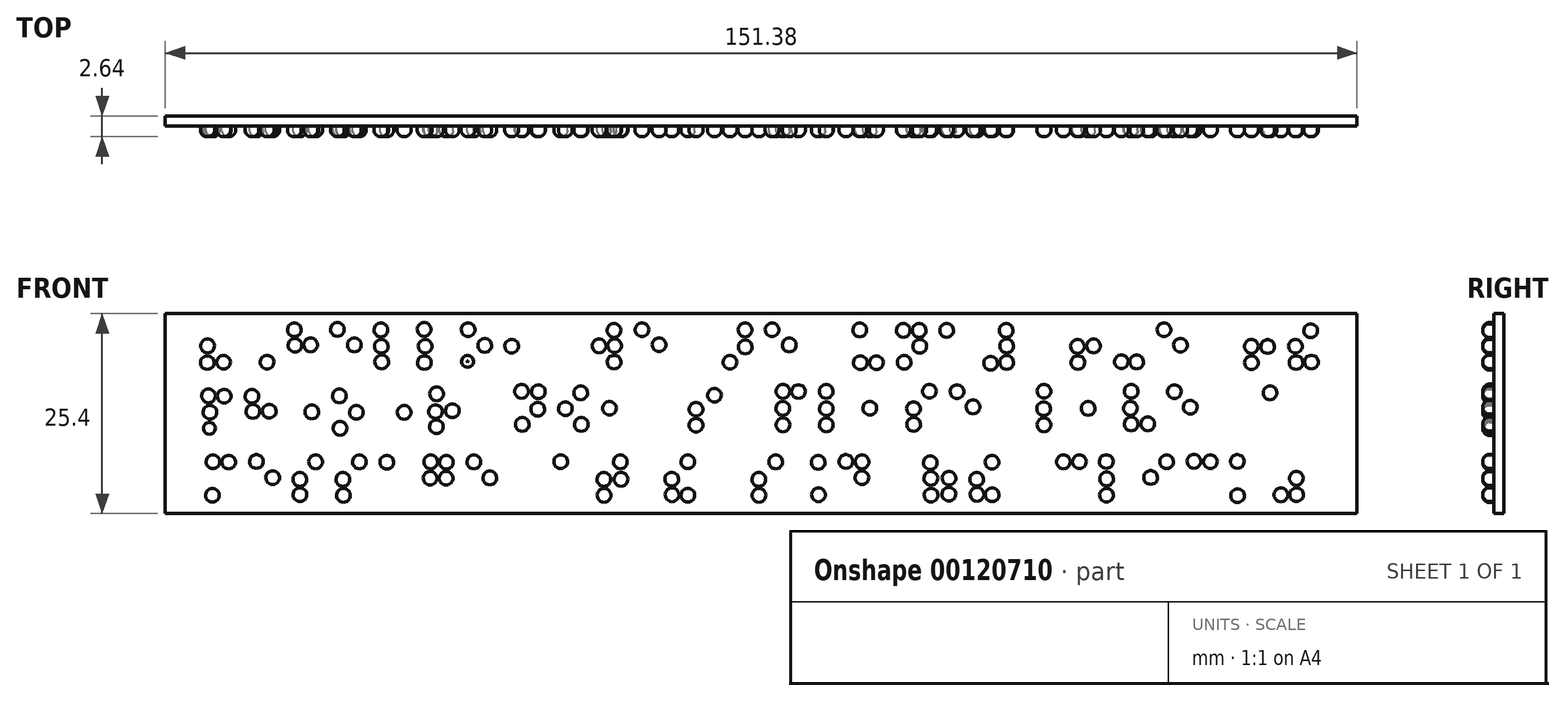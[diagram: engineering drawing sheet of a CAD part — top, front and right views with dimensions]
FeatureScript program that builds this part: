
annotation { "Feature Type Name" : "Feature", "Feature Type Description" : "" }
export const myFeature = defineFeature(function(context is Context, id is Id, definition is map)
    precondition{}
    {
        {
            var Q0;
            Q0=qCreatedBy(makeId("Front.planeOp"),FACE);
            var sketch = newSketch(context, id + "F0", { "sketchPlane" : qUnion([Q0])});
            skCircle(sketch, "E0", {"center": v(-69.31, 93.37) * mm, "radius": 0.76 * mm});
            skCircle(sketch, "E1", {"center": v(-69.35, 91.54) * mm, "radius": 0.76 * mm});
            skCircle(sketch, "E2", {"center": v(-67.56, 91.57) * mm, "radius": 0.76 * mm});
            skCircle(sketch, "E3", {"center": v(-62.75, 91.6) * mm, "radius": 0.76 * mm});
            skCircle(sketch, "E4", {"center": v(-59.66, 93.46) * mm, "radius": 0.76 * mm});
            skCircle(sketch, "E5", {"center": v(-57.93, 93.48) * mm, "radius": 0.76 * mm});
            skCircle(sketch, "E6", {"center": v(-59.73, 95.18) * mm, "radius": 0.76 * mm});
            skCircle(sketch, "E7", {"center": v(-54.97, 95.2) * mm, "radius": 0.76 * mm});
            skCircle(sketch, "E8", {"center": v(-53.1, 93.48) * mm, "radius": 0.76 * mm});
            skCircle(sketch, "E9", {"center": v(-50.17, 95.15) * mm, "radius": 0.76 * mm});
            skCircle(sketch, "E10", {"center": v(-50.13, 93.34) * mm, "radius": 0.76 * mm});
            skCircle(sketch, "E11", {"center": v(-50.08, 91.6) * mm, "radius": 0.76 * mm});
            skCircle(sketch, "E12", {"center": v(-45.39, 95.2) * mm, "radius": 0.76 * mm});
            skCircle(sketch, "E13", {"center": v(-45.28, 93.34) * mm, "radius": 0.76 * mm});
            skCircle(sketch, "E14", {"center": v(-45.37, 91.54) * mm, "radius": 0.76 * mm});
            skCircle(sketch, "E15", {"center": v(-40.54, 95.18) * mm, "radius": 0.76 * mm});
            skCircle(sketch, "E16", {"center": v(-38.7, 93.43) * mm, "radius": 0.76 * mm});
            skCircle(sketch, "E17", {"center": v(-40.6, 91.67) * mm, "radius": 0.66 * mm});
            skCircle(sketch, "E18", {"center": v(-35.73, 93.35) * mm, "radius": 0.76 * mm});
            skLineSegment(sketch, "E19", {"start": v(-70.58, 102.86) * mm, "end": v(80.8, 102.86) * mm});
            skCircle(sketch, "E20", {"center": v(-24.43, 95.09) * mm, "radius": 0.76 * mm});
            skCircle(sketch, "E21", {"center": v(-24.36, 93.4) * mm, "radius": 0.76 * mm});
            skCircle(sketch, "E22", {"center": v(-26.07, 93.37) * mm, "radius": 0.76 * mm});
            skCircle(sketch, "E23", {"center": v(-24.4, 91.6) * mm, "radius": 0.76 * mm});
            skCircle(sketch, "E24", {"center": v(-21.34, 95.16) * mm, "radius": 0.76 * mm});
            skCircle(sketch, "E25", {"center": v(-19.45, 93.51) * mm, "radius": 0.76 * mm});
            skCircle(sketch, "E26", {"center": v(-9.93, 93.28) * mm, "radius": 0.76 * mm});
            skCircle(sketch, "E27", {"center": v(-9.95, 95.14) * mm, "radius": 0.76 * mm});
            skCircle(sketch, "E28", {"center": v(-11.62, 91.58) * mm, "radius": 0.76 * mm});
            skCircle(sketch, "E29", {"center": v(-6.96, 95.16) * mm, "radius": 0.76 * mm});
            skCircle(sketch, "E30", {"center": v(-5.06, 93.48) * mm, "radius": 0.76 * mm});
            skCircle(sketch, "E31", {"center": v(2.72, 95.15) * mm, "radius": 0.76 * mm});
            skCircle(sketch, "E32", {"center": v(2.79, 91.53) * mm, "radius": 0.76 * mm});
            skCircle(sketch, "E33", {"center": v(4.56, 91.53) * mm, "radius": 0.76 * mm});
            skCircle(sketch, "E34", {"center": v(7.54, 95.08) * mm, "radius": 0.76 * mm});
            skCircle(sketch, "E35", {"center": v(9.28, 95.1) * mm, "radius": 0.76 * mm});
            skCircle(sketch, "E36", {"center": v(9.35, 93.35) * mm, "radius": 0.76 * mm});
            skCircle(sketch, "E37", {"center": v(7.63, 91.58) * mm, "radius": 0.76 * mm});
            skCircle(sketch, "E38", {"center": v(12.32, 95.08) * mm, "radius": 0.76 * mm});
            skCircle(sketch, "E39", {"center": v(18.9, 95.08) * mm, "radius": 0.76 * mm});
            skCircle(sketch, "E40", {"center": v(18.95, 93.38) * mm, "radius": 0.76 * mm});
            skCircle(sketch, "E41", {"center": v(18.95, 91.56) * mm, "radius": 0.76 * mm});
            skCircle(sketch, "E42", {"center": v(17.18, 91.48) * mm, "radius": 0.76 * mm});
            skCircle(sketch, "E43", {"center": v(26.78, 93.33) * mm, "radius": 0.76 * mm});
            skCircle(sketch, "E44", {"center": v(28.55, 93.36) * mm, "radius": 0.76 * mm});
            skCircle(sketch, "E45", {"center": v(26.82, 91.54) * mm, "radius": 0.76 * mm});
            skCircle(sketch, "E46", {"center": v(31.62, 91.63) * mm, "radius": 0.76 * mm});
            skCircle(sketch, "E47", {"center": v(33.3, 91.61) * mm, "radius": 0.76 * mm});
            skCircle(sketch, "E48", {"center": v(36.33, 95.16) * mm, "radius": 0.76 * mm});
            skCircle(sketch, "E49", {"center": v(38.15, 93.46) * mm, "radius": 0.76 * mm});
            skCircle(sketch, "E50", {"center": v(45.97, 93.33) * mm, "radius": 0.76 * mm});
            skCircle(sketch, "E51", {"center": v(46, 91.52) * mm, "radius": 0.76 * mm});
            skCircle(sketch, "E52", {"center": v(47.78, 93.3) * mm, "radius": 0.76 * mm});
            skCircle(sketch, "E53", {"center": v(50.85, 93.35) * mm, "radius": 0.76 * mm});
            skCircle(sketch, "E54", {"center": v(52.53, 95.06) * mm, "radius": 0.76 * mm});
            skCircle(sketch, "E55", {"center": v(50.92, 91.54) * mm, "radius": 0.76 * mm});
            skCircle(sketch, "E56", {"center": v(52.62, 91.6) * mm, "radius": 0.76 * mm});
            skCircle(sketch, "E57", {"center": v(-69.18, 86.5) * mm, "radius": 0.76 * mm});
            skCircle(sketch, "E58", {"center": v(-69.02, 84.7) * mm, "radius": 0.76 * mm});
            skCircle(sketch, "E59", {"center": v(-69.08, 82.91) * mm, "radius": 0.76 * mm});
            skCircle(sketch, "E60", {"center": v(-67.45, 86.47) * mm, "radius": 0.76 * mm});
            skCircle(sketch, "E61", {"center": v(-64.38, 86.45) * mm, "radius": 0.76 * mm});
            skCircle(sketch, "E62", {"center": v(-64.28, 84.77) * mm, "radius": 0.76 * mm});
            skCircle(sketch, "E63", {"center": v(-62.47, 84.81) * mm, "radius": 0.76 * mm});
            skCircle(sketch, "E64", {"center": v(-57.77, 84.73) * mm, "radius": 0.76 * mm});
            skCircle(sketch, "E65", {"center": v(-54.72, 86.5) * mm, "radius": 0.76 * mm});
            skCircle(sketch, "E66", {"center": v(-52.85, 84.68) * mm, "radius": 0.76 * mm});
            skCircle(sketch, "E67", {"center": v(-54.66, 82.9) * mm, "radius": 0.76 * mm});
            skCircle(sketch, "E68", {"center": v(-47.57, 84.66) * mm, "radius": 0.76 * mm});
            skCircle(sketch, "E69", {"center": v(-44.1, 84.76) * mm, "radius": 0.76 * mm});
            skCircle(sketch, "E70", {"center": v(-43.98, 86.72) * mm, "radius": 0.76 * mm});
            skCircle(sketch, "E71", {"center": v(-42.25, 84.86) * mm, "radius": 0.76 * mm});
            skCircle(sketch, "E72", {"center": v(-44, 83.1) * mm, "radius": 0.76 * mm});
            skCircle(sketch, "E73", {"center": v(-34.6, 86.99) * mm, "radius": 0.76 * mm});
            skCircle(sketch, "E74", {"center": v(-32.74, 86.97) * mm, "radius": 0.76 * mm});
            skCircle(sketch, "E75", {"center": v(-32.82, 85.03) * mm, "radius": 0.76 * mm});
            skCircle(sketch, "E76", {"center": v(-34.53, 83.35) * mm, "radius": 0.76 * mm});
            skCircle(sketch, "E77", {"center": v(-29.76, 85.08) * mm, "radius": 0.76 * mm});
            skCircle(sketch, "E78", {"center": v(-28.07, 86.83) * mm, "radius": 0.76 * mm});
            skCircle(sketch, "E79", {"center": v(-28, 83.35) * mm, "radius": 0.76 * mm});
            skCircle(sketch, "E80", {"center": v(-24.9, 85.13) * mm, "radius": 0.76 * mm});
            skCircle(sketch, "E81", {"center": v(-13.3, 86.57) * mm, "radius": 0.76 * mm});
            skCircle(sketch, "E82", {"center": v(-15.33, 85.01) * mm, "radius": 0.76 * mm});
            skCircle(sketch, "E83", {"center": v(-15.33, 83.27) * mm, "radius": 0.76 * mm});
            skCircle(sketch, "E84", {"center": v(-5.73, 87) * mm, "radius": 0.76 * mm});
            skCircle(sketch, "E85", {"center": v(-4.02, 86.97) * mm, "radius": 0.76 * mm});
            skCircle(sketch, "E86", {"center": v(-5.75, 85.11) * mm, "radius": 0.76 * mm});
            skCircle(sketch, "E87", {"center": v(-5.73, 83.29) * mm, "radius": 0.76 * mm});
            skCircle(sketch, "E88", {"center": v(-0.96, 87) * mm, "radius": 0.76 * mm});
            skCircle(sketch, "E89", {"center": v(-0.94, 85.07) * mm, "radius": 0.76 * mm});
            skCircle(sketch, "E90", {"center": v(-0.94, 83.29) * mm, "radius": 0.76 * mm});
            skCircle(sketch, "E91", {"center": v(3.87, 85.14) * mm, "radius": 0.76 * mm});
            skCircle(sketch, "E92", {"center": v(8.69, 85.08) * mm, "radius": 0.76 * mm});
            skCircle(sketch, "E93", {"center": v(8.7, 83.35) * mm, "radius": 0.76 * mm});
            skCircle(sketch, "E94", {"center": v(10.45, 87) * mm, "radius": 0.76 * mm});
            skCircle(sketch, "E95", {"center": v(13.5, 86.97) * mm, "radius": 0.76 * mm});
            skCircle(sketch, "E96", {"center": v(15.26, 85.27) * mm, "radius": 0.76 * mm});
            skCircle(sketch, "E97", {"center": v(23.1, 87.01) * mm, "radius": 0.76 * mm});
            skCircle(sketch, "E98", {"center": v(23.07, 85.1) * mm, "radius": 0.76 * mm});
            skCircle(sketch, "E99", {"center": v(23.1, 83.29) * mm, "radius": 0.76 * mm});
            skCircle(sketch, "E100", {"center": v(27.98, 85.12) * mm, "radius": 0.76 * mm});
            skCircle(sketch, "E101", {"center": v(32.74, 87.03) * mm, "radius": 0.76 * mm});
            skCircle(sketch, "E102", {"center": v(32.65, 85.1) * mm, "radius": 0.76 * mm});
            skCircle(sketch, "E103", {"center": v(32.74, 83.4) * mm, "radius": 0.76 * mm});
            skCircle(sketch, "E104", {"center": v(34.57, 83.4) * mm, "radius": 0.76 * mm});
            skCircle(sketch, "E105", {"center": v(37.5, 86.97) * mm, "radius": 0.76 * mm});
            skCircle(sketch, "E106", {"center": v(39.26, 85.25) * mm, "radius": 0.76 * mm});
            skCircle(sketch, "E107", {"center": v(48.07, 86.83) * mm, "radius": 0.76 * mm});
            skCircle(sketch, "E108", {"center": v(-68.65, 78.1) * mm, "radius": 0.76 * mm});
            skCircle(sketch, "E109", {"center": v(-68.7, 74.42) * mm, "radius": 0.76 * mm});
            skCircle(sketch, "E110", {"center": v(-66.9, 78.08) * mm, "radius": 0.76 * mm});
            skCircle(sketch, "E111", {"center": v(-63.84, 78.14) * mm, "radius": 0.76 * mm});
            skCircle(sketch, "E112", {"center": v(-62.05, 76.36) * mm, "radius": 0.76 * mm});
            skCircle(sketch, "E113", {"center": v(-59.05, 76.17) * mm, "radius": 0.76 * mm});
            skCircle(sketch, "E114", {"center": v(-59.03, 74.49) * mm, "radius": 0.76 * mm});
            skCircle(sketch, "E115", {"center": v(-57.3, 78.1) * mm, "radius": 0.76 * mm});
            skCircle(sketch, "E116", {"center": v(-54.3, 76.16) * mm, "radius": 0.76 * mm});
            skCircle(sketch, "E117", {"center": v(-54.23, 74.4) * mm, "radius": 0.76 * mm});
            skCircle(sketch, "E118", {"center": v(-52.47, 78.1) * mm, "radius": 0.76 * mm});
            skCircle(sketch, "E119", {"center": v(-49.44, 78.07) * mm, "radius": 0.76 * mm});
            skCircle(sketch, "E120", {"center": v(-44.59, 78.09) * mm, "radius": 0.76 * mm});
            skCircle(sketch, "E121", {"center": v(-42.86, 78.06) * mm, "radius": 0.76 * mm});
            skCircle(sketch, "E122", {"center": v(-42.9, 76.3) * mm, "radius": 0.76 * mm});
            skCircle(sketch, "E123", {"center": v(-44.65, 76.3) * mm, "radius": 0.76 * mm});
            skCircle(sketch, "E124", {"center": v(-39.82, 78.09) * mm, "radius": 0.76 * mm});
            skCircle(sketch, "E125", {"center": v(-38.06, 76.33) * mm, "radius": 0.76 * mm});
            skCircle(sketch, "E126", {"center": v(-30.23, 78.12) * mm, "radius": 0.76 * mm});
            skCircle(sketch, "E127", {"center": v(-23.64, 78.09) * mm, "radius": 0.76 * mm});
            skCircle(sketch, "E128", {"center": v(-23.57, 76.16) * mm, "radius": 0.76 * mm});
            skCircle(sketch, "E129", {"center": v(-25.47, 76.16) * mm, "radius": 0.76 * mm});
            skCircle(sketch, "E130", {"center": v(-25.43, 74.4) * mm, "radius": 0.76 * mm});
            skCircle(sketch, "E131", {"center": v(-17.93, 74.46) * mm, "radius": 0.76 * mm});
            skCircle(sketch, "E132", {"center": v(-16.19, 74.42) * mm, "radius": 0.76 * mm});
            skCircle(sketch, "E133", {"center": v(-17.97, 76.19) * mm, "radius": 0.76 * mm});
            skCircle(sketch, "E134", {"center": v(-16.19, 78.1) * mm, "radius": 0.76 * mm});
            skCircle(sketch, "E135", {"center": v(-6.48, 78.1) * mm, "radius": 0.76 * mm});
            skCircle(sketch, "E136", {"center": v(-8.35, 76.15) * mm, "radius": 0.76 * mm});
            skCircle(sketch, "E137", {"center": v(-8.33, 74.4) * mm, "radius": 0.76 * mm});
            skCircle(sketch, "E138", {"center": v(-1.79, 78.03) * mm, "radius": 0.76 * mm});
            skCircle(sketch, "E139", {"center": v(-1.75, 74.46) * mm, "radius": 0.76 * mm});
            skCircle(sketch, "E140", {"center": v(1.28, 78.14) * mm, "radius": 0.76 * mm});
            skCircle(sketch, "E141", {"center": v(3.06, 78.1) * mm, "radius": 0.76 * mm});
            skCircle(sketch, "E142", {"center": v(3.03, 76.34) * mm, "radius": 0.76 * mm});
            skCircle(sketch, "E143", {"center": v(10.6, 78) * mm, "radius": 0.76 * mm});
            skCircle(sketch, "E144", {"center": v(10.65, 76.27) * mm, "radius": 0.76 * mm});
            skCircle(sketch, "E145", {"center": v(12.66, 76.3) * mm, "radius": 0.76 * mm});
            skCircle(sketch, "E146", {"center": v(12.64, 74.54) * mm, "radius": 0.76 * mm});
            skCircle(sketch, "E147", {"center": v(10.68, 74.43) * mm, "radius": 0.76 * mm});
            skCircle(sketch, "E148", {"center": v(17.41, 78.06) * mm, "radius": 0.76 * mm});
            skCircle(sketch, "E149", {"center": v(15.72, 76.17) * mm, "radius": 0.76 * mm});
            skCircle(sketch, "E150", {"center": v(15.75, 74.5) * mm, "radius": 0.76 * mm});
            skCircle(sketch, "E151", {"center": v(17.43, 74.46) * mm, "radius": 0.76 * mm});
            skCircle(sketch, "E152", {"center": v(25.3, 78.1) * mm, "radius": 0.76 * mm});
            skCircle(sketch, "E153", {"center": v(27.06, 78.1) * mm, "radius": 0.76 * mm});
            skCircle(sketch, "E154", {"center": v(30.04, 78.13) * mm, "radius": 0.76 * mm});
            skCircle(sketch, "E155", {"center": v(30.07, 76.21) * mm, "radius": 0.76 * mm});
            skCircle(sketch, "E156", {"center": v(30.06, 74.4) * mm, "radius": 0.76 * mm});
            skCircle(sketch, "E157", {"center": v(34.93, 76.37) * mm, "radius": 0.76 * mm});
            skCircle(sketch, "E158", {"center": v(36.7, 78.12) * mm, "radius": 0.76 * mm});
            skCircle(sketch, "E159", {"center": v(39.72, 78.16) * mm, "radius": 0.76 * mm});
            skCircle(sketch, "E160", {"center": v(41.53, 78.12) * mm, "radius": 0.76 * mm});
            skCircle(sketch, "E161", {"center": v(44.51, 78.14) * mm, "radius": 0.76 * mm});
            skCircle(sketch, "E162", {"center": v(44.53, 74.38) * mm, "radius": 0.76 * mm});
            skCircle(sketch, "E163", {"center": v(49.32, 74.46) * mm, "radius": 0.76 * mm});
            skCircle(sketch, "E164", {"center": v(51.05, 74.48) * mm, "radius": 0.76 * mm});
            skCircle(sketch, "E165", {"center": v(51.03, 76.27) * mm, "radius": 0.76 * mm});
            skSolve(sketch);
        }
        {
            var Q0;
            Q0=makeQuery(id+"F0.imprint","IMPRINT",FACE,{"disambiguationData":[TD([[makeQuery(id+"F0.imprint","IMPRINT",EDGE,{"derivedFrom":sQuery(id+"F0.wireOp",EDGE,"E88")}),1.0]])]});
            var Q1;
            Q1=makeQuery(id+"F0.imprint","IMPRINT",FACE,{"disambiguationData":[TD([[makeQuery(id+"F0.imprint","IMPRINT",EDGE,{"derivedFrom":sQuery(id+"F0.wireOp",EDGE,"E24")}),1.0]])]});
            var Q2;
            Q2=makeQuery(id+"F0.imprint","IMPRINT",FACE,{"disambiguationData":[TD([[makeQuery(id+"F0.imprint","IMPRINT",EDGE,{"derivedFrom":sQuery(id+"F0.wireOp",EDGE,"E135")}),1.0]])]});
            var Q3;
            Q3=makeQuery(id+"F0.imprint","IMPRINT",FACE,{"disambiguationData":[TD([[makeQuery(id+"F0.imprint","IMPRINT",EDGE,{"derivedFrom":sQuery(id+"F0.wireOp",EDGE,"E14")}),1.0]])]});
            var Q4;
            Q4=makeQuery(id+"F0.imprint","IMPRINT",FACE,{"disambiguationData":[TD([[makeQuery(id+"F0.imprint","IMPRINT",EDGE,{"derivedFrom":sQuery(id+"F0.wireOp",EDGE,"E13")}),1.0]])]});
            var Q5;
            Q5=makeQuery(id+"F0.imprint","IMPRINT",FACE,{"disambiguationData":[TD([[makeQuery(id+"F0.imprint","IMPRINT",EDGE,{"derivedFrom":sQuery(id+"F0.wireOp",EDGE,"E36")}),1.0]])]});
            var Q6;
            Q6=makeQuery(id+"F0.imprint","IMPRINT",FACE,{"disambiguationData":[TD([[makeQuery(id+"F0.imprint","IMPRINT",EDGE,{"derivedFrom":sQuery(id+"F0.wireOp",EDGE,"E52")}),1.0]])]});
            var Q7;
            Q7=makeQuery(id+"F0.imprint","IMPRINT",FACE,{"disambiguationData":[TD([[makeQuery(id+"F0.imprint","IMPRINT",EDGE,{"derivedFrom":sQuery(id+"F0.wireOp",EDGE,"E40")}),1.0]])]});
            var Q8;
            Q8=makeQuery(id+"F0.imprint","IMPRINT",FACE,{"disambiguationData":[TD([[makeQuery(id+"F0.imprint","IMPRINT",EDGE,{"derivedFrom":sQuery(id+"F0.wireOp",EDGE,"E72")}),1.0]])]});
            var Q9;
            Q9=makeQuery(id+"F0.imprint","IMPRINT",FACE,{"disambiguationData":[TD([[makeQuery(id+"F0.imprint","IMPRINT",EDGE,{"derivedFrom":sQuery(id+"F0.wireOp",EDGE,"E20")}),1.0]])]});
            var Q10;
            Q10=makeQuery(id+"F0.imprint","IMPRINT",FACE,{"disambiguationData":[TD([[makeQuery(id+"F0.imprint","IMPRINT",EDGE,{"derivedFrom":sQuery(id+"F0.wireOp",EDGE,"E100")}),1.0]])]});
            var Q11;
            Q11=makeQuery(id+"F0.imprint","IMPRINT",FACE,{"disambiguationData":[TD([[makeQuery(id+"F0.imprint","IMPRINT",EDGE,{"derivedFrom":sQuery(id+"F0.wireOp",EDGE,"E21")}),1.0]])]});
            var Q12;
            Q12=makeQuery(id+"F0.imprint","IMPRINT",FACE,{"disambiguationData":[TD([[makeQuery(id+"F0.imprint","IMPRINT",EDGE,{"derivedFrom":sQuery(id+"F0.wireOp",EDGE,"E117")}),1.0]])]});
            var Q13;
            Q13=makeQuery(id+"F0.imprint","IMPRINT",FACE,{"disambiguationData":[TD([[makeQuery(id+"F0.imprint","IMPRINT",EDGE,{"derivedFrom":sQuery(id+"F0.wireOp",EDGE,"E152")}),1.0]])]});
            var Q14;
            Q14=makeQuery(id+"F0.imprint","IMPRINT",FACE,{"disambiguationData":[TD([[makeQuery(id+"F0.imprint","IMPRINT",EDGE,{"derivedFrom":sQuery(id+"F0.wireOp",EDGE,"E84")}),1.0]])]});
            var Q15;
            Q15=makeQuery(id+"F0.imprint","IMPRINT",FACE,{"disambiguationData":[TD([[makeQuery(id+"F0.imprint","IMPRINT",EDGE,{"derivedFrom":sQuery(id+"F0.wireOp",EDGE,"E101")}),1.0]])]});
            var Q16;
            Q16=makeQuery(id+"F0.imprint","IMPRINT",FACE,{"disambiguationData":[TD([[makeQuery(id+"F0.imprint","IMPRINT",EDGE,{"derivedFrom":sQuery(id+"F0.wireOp",EDGE,"E35")}),1.0]])]});
            var Q17;
            Q17=makeQuery(id+"F0.imprint","IMPRINT",FACE,{"disambiguationData":[TD([[makeQuery(id+"F0.imprint","IMPRINT",EDGE,{"derivedFrom":sQuery(id+"F0.wireOp",EDGE,"E18")}),1.0]])]});
            var Q18;
            Q18=makeQuery(id+"F0.imprint","IMPRINT",FACE,{"disambiguationData":[TD([[makeQuery(id+"F0.imprint","IMPRINT",EDGE,{"derivedFrom":sQuery(id+"F0.wireOp",EDGE,"E4")}),1.0]])]});
            var Q19;
            Q19=makeQuery(id+"F0.imprint","IMPRINT",FACE,{"disambiguationData":[TD([[makeQuery(id+"F0.imprint","IMPRINT",EDGE,{"derivedFrom":sQuery(id+"F0.wireOp",EDGE,"E134")}),1.0]])]});
            var Q20;
            Q20=makeQuery(id+"F0.imprint","IMPRINT",FACE,{"disambiguationData":[TD([[makeQuery(id+"F0.imprint","IMPRINT",EDGE,{"derivedFrom":sQuery(id+"F0.wireOp",EDGE,"E69")}),1.0]])]});
            var Q21;
            Q21=makeQuery(id+"F0.imprint","IMPRINT",FACE,{"disambiguationData":[TD([[makeQuery(id+"F0.imprint","IMPRINT",EDGE,{"derivedFrom":sQuery(id+"F0.wireOp",EDGE,"E70")}),1.0]])]});
            var Q22;
            Q22=makeQuery(id+"F0.imprint","IMPRINT",FACE,{"disambiguationData":[TD([[makeQuery(id+"F0.imprint","IMPRINT",EDGE,{"derivedFrom":sQuery(id+"F0.wireOp",EDGE,"E89")}),1.0]])]});
            var Q23;
            Q23=makeQuery(id+"F0.imprint","IMPRINT",FACE,{"disambiguationData":[TD([[makeQuery(id+"F0.imprint","IMPRINT",EDGE,{"derivedFrom":sQuery(id+"F0.wireOp",EDGE,"E57")}),1.0]])]});
            var Q24;
            Q24=makeQuery(id+"F0.imprint","IMPRINT",FACE,{"disambiguationData":[TD([[makeQuery(id+"F0.imprint","IMPRINT",EDGE,{"derivedFrom":sQuery(id+"F0.wireOp",EDGE,"E86")}),1.0]])]});
            var Q25;
            Q25=makeQuery(id+"F0.imprint","IMPRINT",FACE,{"disambiguationData":[TD([[makeQuery(id+"F0.imprint","IMPRINT",EDGE,{"derivedFrom":sQuery(id+"F0.wireOp",EDGE,"E102")}),1.0]])]});
            var Q26;
            Q26=makeQuery(id+"F0.imprint","IMPRINT",FACE,{"disambiguationData":[TD([[makeQuery(id+"F0.imprint","IMPRINT",EDGE,{"derivedFrom":sQuery(id+"F0.wireOp",EDGE,"E149")}),1.0]])]});
            var Q27;
            Q27=makeQuery(id+"F0.imprint","IMPRINT",FACE,{"disambiguationData":[TD([[makeQuery(id+"F0.imprint","IMPRINT",EDGE,{"derivedFrom":sQuery(id+"F0.wireOp",EDGE,"E153")}),1.0]])]});
            var Q28;
            Q28=makeQuery(id+"F0.imprint","IMPRINT",FACE,{"disambiguationData":[TD([[makeQuery(id+"F0.imprint","IMPRINT",EDGE,{"derivedFrom":sQuery(id+"F0.wireOp",EDGE,"E82")}),1.0]])]});
            var Q29;
            Q29=makeQuery(id+"F0.imprint","IMPRINT",FACE,{"disambiguationData":[TD([[makeQuery(id+"F0.imprint","IMPRINT",EDGE,{"derivedFrom":sQuery(id+"F0.wireOp",EDGE,"E54")}),1.0]])]});
            var Q30;
            Q30=makeQuery(id+"F0.imprint","IMPRINT",FACE,{"disambiguationData":[TD([[makeQuery(id+"F0.imprint","IMPRINT",EDGE,{"derivedFrom":sQuery(id+"F0.wireOp",EDGE,"E133")}),1.0]])]});
            var Q31;
            Q31=makeQuery(id+"F0.imprint","IMPRINT",FACE,{"disambiguationData":[TD([[makeQuery(id+"F0.imprint","IMPRINT",EDGE,{"derivedFrom":sQuery(id+"F0.wireOp",EDGE,"E105")}),1.0]])]});
            var Q32;
            Q32=makeQuery(id+"F0.imprint","IMPRINT",FACE,{"disambiguationData":[TD([[makeQuery(id+"F0.imprint","IMPRINT",EDGE,{"derivedFrom":sQuery(id+"F0.wireOp",EDGE,"E6")}),1.0]])]});
            var Q33;
            Q33=makeQuery(id+"F0.imprint","IMPRINT",FACE,{"disambiguationData":[TD([[makeQuery(id+"F0.imprint","IMPRINT",EDGE,{"derivedFrom":sQuery(id+"F0.wireOp",EDGE,"E7")}),1.0]])]});
            var Q34;
            Q34=makeQuery(id+"F0.imprint","IMPRINT",FACE,{"disambiguationData":[TD([[makeQuery(id+"F0.imprint","IMPRINT",EDGE,{"derivedFrom":sQuery(id+"F0.wireOp",EDGE,"E50")}),1.0]])]});
            var Q35;
            Q35=makeQuery(id+"F0.imprint","IMPRINT",FACE,{"disambiguationData":[TD([[makeQuery(id+"F0.imprint","IMPRINT",EDGE,{"derivedFrom":sQuery(id+"F0.wireOp",EDGE,"E9")}),1.0]])]});
            var Q36;
            Q36=makeQuery(id+"F0.imprint","IMPRINT",FACE,{"disambiguationData":[TD([[makeQuery(id+"F0.imprint","IMPRINT",EDGE,{"derivedFrom":sQuery(id+"F0.wireOp",EDGE,"E10")}),1.0]])]});
            var Q37;
            Q37=makeQuery(id+"F0.imprint","IMPRINT",FACE,{"disambiguationData":[TD([[makeQuery(id+"F0.imprint","IMPRINT",EDGE,{"derivedFrom":sQuery(id+"F0.wireOp",EDGE,"E65")}),1.0]])]});
            var Q38;
            Q38=makeQuery(id+"F0.imprint","IMPRINT",FACE,{"disambiguationData":[TD([[makeQuery(id+"F0.imprint","IMPRINT",EDGE,{"derivedFrom":sQuery(id+"F0.wireOp",EDGE,"E161")}),1.0]])]});
            var Q39;
            Q39=makeQuery(id+"F0.imprint","IMPRINT",FACE,{"disambiguationData":[TD([[makeQuery(id+"F0.imprint","IMPRINT",EDGE,{"derivedFrom":sQuery(id+"F0.wireOp",EDGE,"E97")}),1.0]])]});
            var Q40;
            Q40=makeQuery(id+"F0.imprint","IMPRINT",FACE,{"disambiguationData":[TD([[makeQuery(id+"F0.imprint","IMPRINT",EDGE,{"derivedFrom":sQuery(id+"F0.wireOp",EDGE,"E16")}),1.0]])]});
            var Q41;
            Q41=makeQuery(id+"F0.imprint","IMPRINT",FACE,{"disambiguationData":[TD([[makeQuery(id+"F0.imprint","IMPRINT",EDGE,{"derivedFrom":sQuery(id+"F0.wireOp",EDGE,"E12")}),1.0]])]});
            var Q42;
            Q42=makeQuery(id+"F0.imprint","IMPRINT",FACE,{"disambiguationData":[TD([[makeQuery(id+"F0.imprint","IMPRINT",EDGE,{"derivedFrom":sQuery(id+"F0.wireOp",EDGE,"E74")}),1.0]])]});
            var Q43;
            Q43=makeQuery(id+"F0.imprint","IMPRINT",FACE,{"disambiguationData":[TD([[makeQuery(id+"F0.imprint","IMPRINT",EDGE,{"derivedFrom":sQuery(id+"F0.wireOp",EDGE,"E48")}),1.0]])]});
            var Q44;
            Q44=makeQuery(id+"F0.imprint","IMPRINT",FACE,{"disambiguationData":[TD([[makeQuery(id+"F0.imprint","IMPRINT",EDGE,{"derivedFrom":sQuery(id+"F0.wireOp",EDGE,"E125")}),1.0]])]});
            var Q45;
            Q45=makeQuery(id+"F0.imprint","IMPRINT",FACE,{"disambiguationData":[TD([[makeQuery(id+"F0.imprint","IMPRINT",EDGE,{"derivedFrom":sQuery(id+"F0.wireOp",EDGE,"E61")}),1.0]])]});
            var Q46;
            Q46=makeQuery(id+"F0.imprint","IMPRINT",FACE,{"disambiguationData":[TD([[makeQuery(id+"F0.imprint","IMPRINT",EDGE,{"derivedFrom":sQuery(id+"F0.wireOp",EDGE,"E29")}),1.0]])]});
            var Q47;
            Q47=makeQuery(id+"F0.imprint","IMPRINT",FACE,{"disambiguationData":[TD([[makeQuery(id+"F0.imprint","IMPRINT",EDGE,{"derivedFrom":sQuery(id+"F0.wireOp",EDGE,"E143")}),1.0]])]});
            var Q48;
            Q48=makeQuery(id+"F0.imprint","IMPRINT",FACE,{"disambiguationData":[TD([[makeQuery(id+"F0.imprint","IMPRINT",EDGE,{"derivedFrom":sQuery(id+"F0.wireOp",EDGE,"E154")}),1.0]])]});
            var Q49;
            Q49=makeQuery(id+"F0.imprint","IMPRINT",FACE,{"disambiguationData":[TD([[makeQuery(id+"F0.imprint","IMPRINT",EDGE,{"derivedFrom":sQuery(id+"F0.wireOp",EDGE,"E138")}),1.0]])]});
            var Q50;
            Q50=makeQuery(id+"F0.imprint","IMPRINT",FACE,{"disambiguationData":[TD([[makeQuery(id+"F0.imprint","IMPRINT",EDGE,{"derivedFrom":sQuery(id+"F0.wireOp",EDGE,"E112")}),1.0]])]});
            var Q51;
            Q51=makeQuery(id+"F0.imprint","IMPRINT",FACE,{"disambiguationData":[TD([[makeQuery(id+"F0.imprint","IMPRINT",EDGE,{"derivedFrom":sQuery(id+"F0.wireOp",EDGE,"E160")}),1.0]])]});
            var Q52;
            Q52=makeQuery(id+"F0.imprint","IMPRINT",FACE,{"disambiguationData":[TD([[makeQuery(id+"F0.imprint","IMPRINT",EDGE,{"derivedFrom":sQuery(id+"F0.wireOp",EDGE,"E144")}),1.0]])]});
            var Q53;
            Q53=makeQuery(id+"F0.imprint","IMPRINT",FACE,{"disambiguationData":[TD([[makeQuery(id+"F0.imprint","IMPRINT",EDGE,{"derivedFrom":sQuery(id+"F0.wireOp",EDGE,"E27")}),1.0]])]});
            var Q54;
            Q54=makeQuery(id+"F0.imprint","IMPRINT",FACE,{"disambiguationData":[TD([[makeQuery(id+"F0.imprint","IMPRINT",EDGE,{"derivedFrom":sQuery(id+"F0.wireOp",EDGE,"E140")}),1.0]])]});
            var Q55;
            Q55=makeQuery(id+"F0.imprint","IMPRINT",FACE,{"disambiguationData":[TD([[makeQuery(id+"F0.imprint","IMPRINT",EDGE,{"derivedFrom":sQuery(id+"F0.wireOp",EDGE,"E60")}),1.0]])]});
            var Q56;
            Q56=makeQuery(id+"F0.imprint","IMPRINT",FACE,{"disambiguationData":[TD([[makeQuery(id+"F0.imprint","IMPRINT",EDGE,{"derivedFrom":sQuery(id+"F0.wireOp",EDGE,"E75")}),1.0]])]});
            var Q57;
            Q57=makeQuery(id+"F0.imprint","IMPRINT",FACE,{"disambiguationData":[TD([[makeQuery(id+"F0.imprint","IMPRINT",EDGE,{"derivedFrom":sQuery(id+"F0.wireOp",EDGE,"E43")}),1.0]])]});
            var Q58;
            Q58=makeQuery(id+"F0.imprint","IMPRINT",FACE,{"disambiguationData":[TD([[makeQuery(id+"F0.imprint","IMPRINT",EDGE,{"derivedFrom":sQuery(id+"F0.wireOp",EDGE,"E155")}),1.0]])]});
            var Q59;
            Q59=makeQuery(id+"F0.imprint","IMPRINT",FACE,{"disambiguationData":[TD([[makeQuery(id+"F0.imprint","IMPRINT",EDGE,{"derivedFrom":sQuery(id+"F0.wireOp",EDGE,"E123")}),1.0]])]});
            var Q60;
            Q60=makeQuery(id+"F0.imprint","IMPRINT",FACE,{"disambiguationData":[TD([[makeQuery(id+"F0.imprint","IMPRINT",EDGE,{"derivedFrom":sQuery(id+"F0.wireOp",EDGE,"E107")}),1.0]])]});
            var Q61;
            Q61=makeQuery(id+"F0.imprint","IMPRINT",FACE,{"disambiguationData":[TD([[makeQuery(id+"F0.imprint","IMPRINT",EDGE,{"derivedFrom":sQuery(id+"F0.wireOp",EDGE,"E158")}),1.0]])]});
            var Q62;
            Q62=makeQuery(id+"F0.imprint","IMPRINT",FACE,{"disambiguationData":[TD([[makeQuery(id+"F0.imprint","IMPRINT",EDGE,{"derivedFrom":sQuery(id+"F0.wireOp",EDGE,"E78")}),1.0]])]});
            var Q63;
            Q63=makeQuery(id+"F0.imprint","IMPRINT",FACE,{"disambiguationData":[TD([[makeQuery(id+"F0.imprint","IMPRINT",EDGE,{"derivedFrom":sQuery(id+"F0.wireOp",EDGE,"E94")}),1.0]])]});
            var Q64;
            Q64=makeQuery(id+"F0.imprint","IMPRINT",FACE,{"disambiguationData":[TD([[makeQuery(id+"F0.imprint","IMPRINT",EDGE,{"derivedFrom":sQuery(id+"F0.wireOp",EDGE,"E39")}),1.0]])]});
            var Q65;
            Q65=makeQuery(id+"F0.imprint","IMPRINT",FACE,{"disambiguationData":[TD([[makeQuery(id+"F0.imprint","IMPRINT",EDGE,{"derivedFrom":sQuery(id+"F0.wireOp",EDGE,"E55")}),1.0]])]});
            var Q66;
            Q66=makeQuery(id+"F0.imprint","IMPRINT",FACE,{"disambiguationData":[TD([[makeQuery(id+"F0.imprint","IMPRINT",EDGE,{"derivedFrom":sQuery(id+"F0.wireOp",EDGE,"E87")}),1.0]])]});
            var Q67;
            Q67=makeQuery(id+"F0.imprint","IMPRINT",FACE,{"disambiguationData":[TD([[makeQuery(id+"F0.imprint","IMPRINT",EDGE,{"derivedFrom":sQuery(id+"F0.wireOp",EDGE,"E15")}),1.0]])]});
            var Q68;
            Q68=makeQuery(id+"F0.imprint","IMPRINT",FACE,{"disambiguationData":[TD([[makeQuery(id+"F0.imprint","IMPRINT",EDGE,{"derivedFrom":sQuery(id+"F0.wireOp",EDGE,"E71")}),1.0]])]});
            var Q69;
            Q69=makeQuery(id+"F0.imprint","IMPRINT",FACE,{"disambiguationData":[TD([[makeQuery(id+"F0.imprint","IMPRINT",EDGE,{"derivedFrom":sQuery(id+"F0.wireOp",EDGE,"E56")}),1.0]])]});
            var Q70;
            Q70=makeQuery(id+"F0.imprint","IMPRINT",FACE,{"disambiguationData":[TD([[makeQuery(id+"F0.imprint","IMPRINT",EDGE,{"derivedFrom":sQuery(id+"F0.wireOp",EDGE,"E151")}),1.0]])]});
            var Q71;
            Q71=makeQuery(id+"F0.imprint","IMPRINT",FACE,{"disambiguationData":[TD([[makeQuery(id+"F0.imprint","IMPRINT",EDGE,{"derivedFrom":sQuery(id+"F0.wireOp",EDGE,"E103")}),1.0]])]});
            var Q72;
            Q72=makeQuery(id+"F0.imprint","IMPRINT",FACE,{"disambiguationData":[TD([[makeQuery(id+"F0.imprint","IMPRINT",EDGE,{"derivedFrom":sQuery(id+"F0.wireOp",EDGE,"E119")}),1.0]])]});
            var Q73;
            Q73=makeQuery(id+"F0.imprint","IMPRINT",FACE,{"disambiguationData":[TD([[makeQuery(id+"F0.imprint","IMPRINT",EDGE,{"derivedFrom":sQuery(id+"F0.wireOp",EDGE,"E104")}),1.0]])]});
            var Q74;
            Q74=makeQuery(id+"F0.imprint","IMPRINT",FACE,{"disambiguationData":[TD([[makeQuery(id+"F0.imprint","IMPRINT",EDGE,{"derivedFrom":sQuery(id+"F0.wireOp",EDGE,"E0")}),1.0]])]});
            var Q75;
            Q75=makeQuery(id+"F0.imprint","IMPRINT",FACE,{"disambiguationData":[TD([[makeQuery(id+"F0.imprint","IMPRINT",EDGE,{"derivedFrom":sQuery(id+"F0.wireOp",EDGE,"E132")}),1.0]])]});
            var Q76;
            Q76=makeQuery(id+"F0.imprint","IMPRINT",FACE,{"disambiguationData":[TD([[makeQuery(id+"F0.imprint","IMPRINT",EDGE,{"derivedFrom":sQuery(id+"F0.wireOp",EDGE,"E148")}),1.0]])]});
            var Q77;
            Q77=makeQuery(id+"F0.imprint","IMPRINT",FACE,{"disambiguationData":[TD([[makeQuery(id+"F0.imprint","IMPRINT",EDGE,{"derivedFrom":sQuery(id+"F0.wireOp",EDGE,"E2")}),1.0]])]});
            var Q78;
            Q78=makeQuery(id+"F0.imprint","IMPRINT",FACE,{"disambiguationData":[TD([[makeQuery(id+"F0.imprint","IMPRINT",EDGE,{"derivedFrom":sQuery(id+"F0.wireOp",EDGE,"E1")}),1.0]])]});
            var Q79;
            Q79=makeQuery(id+"F0.imprint","IMPRINT",FACE,{"disambiguationData":[TD([[makeQuery(id+"F0.imprint","IMPRINT",EDGE,{"derivedFrom":sQuery(id+"F0.wireOp",EDGE,"E136")}),1.0]])]});
            var Q80;
            Q80=makeQuery(id+"F0.imprint","IMPRINT",FACE,{"disambiguationData":[TD([[makeQuery(id+"F0.imprint","IMPRINT",EDGE,{"derivedFrom":sQuery(id+"F0.wireOp",EDGE,"E120")}),1.0]])]});
            var Q81;
            Q81=makeQuery(id+"F0.imprint","IMPRINT",FACE,{"disambiguationData":[TD([[makeQuery(id+"F0.imprint","IMPRINT",EDGE,{"derivedFrom":sQuery(id+"F0.wireOp",EDGE,"E46")}),1.0]])]});
            var Q82;
            Q82=makeQuery(id+"F0.imprint","IMPRINT",FACE,{"disambiguationData":[TD([[makeQuery(id+"F0.imprint","IMPRINT",EDGE,{"derivedFrom":sQuery(id+"F0.wireOp",EDGE,"E53")}),1.0]])]});
            var Q83;
            Q83=makeQuery(id+"F0.imprint","IMPRINT",FACE,{"disambiguationData":[TD([[makeQuery(id+"F0.imprint","IMPRINT",EDGE,{"derivedFrom":sQuery(id+"F0.wireOp",EDGE,"E164")}),1.0]])]});
            var Q84;
            Q84=makeQuery(id+"F0.imprint","IMPRINT",FACE,{"disambiguationData":[TD([[makeQuery(id+"F0.imprint","IMPRINT",EDGE,{"derivedFrom":sQuery(id+"F0.wireOp",EDGE,"E116")}),1.0]])]});
            var Q85;
            Q85=makeQuery(id+"F0.imprint","IMPRINT",FACE,{"disambiguationData":[TD([[makeQuery(id+"F0.imprint","IMPRINT",EDGE,{"derivedFrom":sQuery(id+"F0.wireOp",EDGE,"E68")}),1.0]])]});
            var Q86;
            Q86=makeQuery(id+"F0.imprint","IMPRINT",FACE,{"disambiguationData":[TD([[makeQuery(id+"F0.imprint","IMPRINT",EDGE,{"derivedFrom":sQuery(id+"F0.wireOp",EDGE,"E37")}),1.0]])]});
            var Q87;
            Q87=makeQuery(id+"F0.imprint","IMPRINT",FACE,{"disambiguationData":[TD([[makeQuery(id+"F0.imprint","IMPRINT",EDGE,{"derivedFrom":sQuery(id+"F0.wireOp",EDGE,"E83")}),1.0]])]});
            var Q88;
            Q88=makeQuery(id+"F0.imprint","IMPRINT",FACE,{"disambiguationData":[TD([[makeQuery(id+"F0.imprint","IMPRINT",EDGE,{"derivedFrom":sQuery(id+"F0.wireOp",EDGE,"E131")}),1.0]])]});
            var Q89;
            Q89=makeQuery(id+"F0.imprint","IMPRINT",FACE,{"disambiguationData":[TD([[makeQuery(id+"F0.imprint","IMPRINT",EDGE,{"derivedFrom":sQuery(id+"F0.wireOp",EDGE,"E147")}),1.0]])]});
            var Q90;
            Q90=makeQuery(id+"F0.imprint","IMPRINT",FACE,{"disambiguationData":[TD([[makeQuery(id+"F0.imprint","IMPRINT",EDGE,{"derivedFrom":sQuery(id+"F0.wireOp",EDGE,"E3")}),1.0]])]});
            var Q91;
            Q91=makeQuery(id+"F0.imprint","IMPRINT",FACE,{"disambiguationData":[TD([[makeQuery(id+"F0.imprint","IMPRINT",EDGE,{"derivedFrom":sQuery(id+"F0.wireOp",EDGE,"E23")}),1.0]])]});
            var Q92;
            Q92=makeQuery(id+"F0.imprint","IMPRINT",FACE,{"disambiguationData":[TD([[makeQuery(id+"F0.imprint","IMPRINT",EDGE,{"derivedFrom":sQuery(id+"F0.wireOp",EDGE,"E67")}),1.0]])]});
            var Q93;
            Q93=makeQuery(id+"F0.imprint","IMPRINT",FACE,{"disambiguationData":[TD([[makeQuery(id+"F0.imprint","IMPRINT",EDGE,{"derivedFrom":sQuery(id+"F0.wireOp",EDGE,"E163")}),1.0]])]});
            var Q94;
            Q94=makeQuery(id+"F0.imprint","IMPRINT",FACE,{"disambiguationData":[TD([[makeQuery(id+"F0.imprint","IMPRINT",EDGE,{"derivedFrom":sQuery(id+"F0.wireOp",EDGE,"E115")}),1.0]])]});
            var Q95;
            Q95=makeQuery(id+"F0.imprint","IMPRINT",FACE,{"disambiguationData":[TD([[makeQuery(id+"F0.imprint","IMPRINT",EDGE,{"derivedFrom":sQuery(id+"F0.wireOp",EDGE,"E99")}),1.0]])]});
            var Q96;
            Q96=makeQuery(id+"F0.imprint","IMPRINT",FACE,{"disambiguationData":[TD([[makeQuery(id+"F0.imprint","IMPRINT",EDGE,{"derivedFrom":sQuery(id+"F0.wireOp",EDGE,"E51")}),1.0]])]});
            var Q97;
            Q97=makeQuery(id+"F0.imprint","IMPRINT",FACE,{"disambiguationData":[TD([[makeQuery(id+"F0.imprint","IMPRINT",EDGE,{"derivedFrom":sQuery(id+"F0.wireOp",EDGE,"E146")}),1.0]])]});
            var Q98;
            Q98=makeQuery(id+"F0.imprint","IMPRINT",FACE,{"disambiguationData":[TD([[makeQuery(id+"F0.imprint","IMPRINT",EDGE,{"derivedFrom":sQuery(id+"F0.wireOp",EDGE,"E130")}),1.0]])]});
            var Q99;
            Q99=makeQuery(id+"F0.imprint","IMPRINT",FACE,{"disambiguationData":[TD([[makeQuery(id+"F0.imprint","IMPRINT",EDGE,{"derivedFrom":sQuery(id+"F0.wireOp",EDGE,"E162")}),1.0]])]});
            var Q100;
            Q100=makeQuery(id+"F0.imprint","IMPRINT",FACE,{"disambiguationData":[TD([[makeQuery(id+"F0.imprint","IMPRINT",EDGE,{"derivedFrom":sQuery(id+"F0.wireOp",EDGE,"E25")}),1.0]])]});
            var Q101;
            Q101=makeQuery(id+"F0.imprint","IMPRINT",FACE,{"disambiguationData":[TD([[makeQuery(id+"F0.imprint","IMPRINT",EDGE,{"derivedFrom":sQuery(id+"F0.wireOp",EDGE,"E150")}),1.0]])]});
            var Q102;
            Q102=makeQuery(id+"F0.imprint","IMPRINT",FACE,{"disambiguationData":[TD([[makeQuery(id+"F0.imprint","IMPRINT",EDGE,{"derivedFrom":sQuery(id+"F0.wireOp",EDGE,"E85")}),1.0]])]});
            var Q103;
            Q103=makeQuery(id+"F0.imprint","IMPRINT",FACE,{"disambiguationData":[TD([[makeQuery(id+"F0.imprint","IMPRINT",EDGE,{"derivedFrom":sQuery(id+"F0.wireOp",EDGE,"E73")}),1.0]])]});
            var Q104;
            Q104=makeQuery(id+"F0.imprint","IMPRINT",FACE,{"disambiguationData":[TD([[makeQuery(id+"F0.imprint","IMPRINT",EDGE,{"derivedFrom":sQuery(id+"F0.wireOp",EDGE,"E5")}),1.0]])]});
            var Q105;
            Q105=makeQuery(id+"F0.imprint","IMPRINT",FACE,{"disambiguationData":[TD([[makeQuery(id+"F0.imprint","IMPRINT",EDGE,{"derivedFrom":sQuery(id+"F0.wireOp",EDGE,"E165")}),1.0]])]});
            var Q106;
            Q106=makeQuery(id+"F0.imprint","IMPRINT",FACE,{"disambiguationData":[TD([[makeQuery(id+"F0.imprint","IMPRINT",EDGE,{"derivedFrom":sQuery(id+"F0.wireOp",EDGE,"E41")}),1.0]])]});
            var Q107;
            Q107=makeQuery(id+"F0.imprint","IMPRINT",FACE,{"disambiguationData":[TD([[makeQuery(id+"F0.imprint","IMPRINT",EDGE,{"derivedFrom":sQuery(id+"F0.wireOp",EDGE,"E22")}),1.0]])]});
            var Q108;
            Q108=makeQuery(id+"F0.imprint","IMPRINT",FACE,{"disambiguationData":[TD([[makeQuery(id+"F0.imprint","IMPRINT",EDGE,{"derivedFrom":sQuery(id+"F0.wireOp",EDGE,"E66")}),1.0]])]});
            var Q109;
            Q109=makeQuery(id+"F0.imprint","IMPRINT",FACE,{"disambiguationData":[TD([[makeQuery(id+"F0.imprint","IMPRINT",EDGE,{"derivedFrom":sQuery(id+"F0.wireOp",EDGE,"E118")}),1.0]])]});
            var Q110;
            Q110=makeQuery(id+"F0.imprint","IMPRINT",FACE,{"disambiguationData":[TD([[makeQuery(id+"F0.imprint","IMPRINT",EDGE,{"derivedFrom":sQuery(id+"F0.wireOp",EDGE,"E38")}),1.0]])]});
            var Q111;
            Q111=makeQuery(id+"F0.imprint","IMPRINT",FACE,{"disambiguationData":[TD([[makeQuery(id+"F0.imprint","IMPRINT",EDGE,{"derivedFrom":sQuery(id+"F0.wireOp",EDGE,"E98")}),1.0]])]});
            var Q112;
            Q112=makeQuery(id+"F0.imprint","IMPRINT",FACE,{"disambiguationData":[TD([[makeQuery(id+"F0.imprint","IMPRINT",EDGE,{"derivedFrom":sQuery(id+"F0.wireOp",EDGE,"E34")}),1.0]])]});
            var Q113;
            Q113=makeQuery(id+"F0.imprint","IMPRINT",FACE,{"disambiguationData":[TD([[makeQuery(id+"F0.imprint","IMPRINT",EDGE,{"derivedFrom":sQuery(id+"F0.wireOp",EDGE,"E137")}),1.0]])]});
            var Q114;
            Q114=makeQuery(id+"F0.imprint","IMPRINT",FACE,{"disambiguationData":[TD([[makeQuery(id+"F0.imprint","IMPRINT",EDGE,{"derivedFrom":sQuery(id+"F0.wireOp",EDGE,"E121")}),1.0]])]});
            var Q115;
            Q115=makeQuery(id+"F0.imprint","IMPRINT",FACE,{"disambiguationData":[TD([[makeQuery(id+"F0.imprint","IMPRINT",EDGE,{"derivedFrom":sQuery(id+"F0.wireOp",EDGE,"E114")}),1.0]])]});
            var Q116;
            Q116=makeQuery(id+"F0.imprint","IMPRINT",FACE,{"disambiguationData":[TD([[makeQuery(id+"F0.imprint","IMPRINT",EDGE,{"derivedFrom":sQuery(id+"F0.wireOp",EDGE,"E17")}),1.0]])]});
            var Q117;
            Q117=makeQuery(id+"F0.imprint","IMPRINT",FACE,{"disambiguationData":[TD([[makeQuery(id+"F0.imprint","IMPRINT",EDGE,{"derivedFrom":sQuery(id+"F0.wireOp",EDGE,"E8")}),1.0]])]});
            var Q118;
            Q118=makeQuery(id+"F0.imprint","IMPRINT",FACE,{"disambiguationData":[TD([[makeQuery(id+"F0.imprint","IMPRINT",EDGE,{"derivedFrom":sQuery(id+"F0.wireOp",EDGE,"E129")}),1.0]])]});
            var Q119;
            Q119=makeQuery(id+"F0.imprint","IMPRINT",FACE,{"disambiguationData":[TD([[makeQuery(id+"F0.imprint","IMPRINT",EDGE,{"derivedFrom":sQuery(id+"F0.wireOp",EDGE,"E145")}),1.0]])]});
            var Q120;
            Q120=makeQuery(id+"F0.imprint","IMPRINT",FACE,{"disambiguationData":[TD([[makeQuery(id+"F0.imprint","IMPRINT",EDGE,{"derivedFrom":sQuery(id+"F0.wireOp",EDGE,"E11")}),1.0]])]});
            var Q121;
            Q121=makeQuery(id+"F0.imprint","IMPRINT",FACE,{"disambiguationData":[TD([[makeQuery(id+"F0.imprint","IMPRINT",EDGE,{"derivedFrom":sQuery(id+"F0.wireOp",EDGE,"E81")}),1.0]])]});
            var Q122;
            Q122=makeQuery(id+"F0.imprint","IMPRINT",FACE,{"disambiguationData":[TD([[makeQuery(id+"F0.imprint","IMPRINT",EDGE,{"derivedFrom":sQuery(id+"F0.wireOp",EDGE,"E113")}),1.0]])]});
            var Q123;
            Q123=makeQuery(id+"F0.imprint","IMPRINT",FACE,{"disambiguationData":[TD([[makeQuery(id+"F0.imprint","IMPRINT",EDGE,{"derivedFrom":sQuery(id+"F0.wireOp",EDGE,"E33")}),1.0]])]});
            var Q124;
            Q124=makeQuery(id+"F0.imprint","IMPRINT",FACE,{"disambiguationData":[TD([[makeQuery(id+"F0.imprint","IMPRINT",EDGE,{"derivedFrom":sQuery(id+"F0.wireOp",EDGE,"E49")}),1.0]])]});
            var Q125;
            Q125=makeQuery(id+"F0.imprint","IMPRINT",FACE,{"disambiguationData":[TD([[makeQuery(id+"F0.imprint","IMPRINT",EDGE,{"derivedFrom":sQuery(id+"F0.wireOp",EDGE,"E26")}),1.0]])]});
            var Q126;
            Q126=makeQuery(id+"F0.imprint","IMPRINT",FACE,{"disambiguationData":[TD([[makeQuery(id+"F0.imprint","IMPRINT",EDGE,{"derivedFrom":sQuery(id+"F0.wireOp",EDGE,"E64")}),1.0]])]});
            var Q127;
            Q127=makeQuery(id+"F0.imprint","IMPRINT",FACE,{"disambiguationData":[TD([[makeQuery(id+"F0.imprint","IMPRINT",EDGE,{"derivedFrom":sQuery(id+"F0.wireOp",EDGE,"E90")}),1.0]])]});
            var Q128;
            Q128=makeQuery(id+"F0.imprint","IMPRINT",FACE,{"disambiguationData":[TD([[makeQuery(id+"F0.imprint","IMPRINT",EDGE,{"derivedFrom":sQuery(id+"F0.wireOp",EDGE,"E109")}),1.0]])]});
            var Q129;
            Q129=makeQuery(id+"F0.imprint","IMPRINT",FACE,{"disambiguationData":[TD([[makeQuery(id+"F0.imprint","IMPRINT",EDGE,{"derivedFrom":sQuery(id+"F0.wireOp",EDGE,"E157")}),1.0]])]});
            var Q130;
            Q130=makeQuery(id+"F0.imprint","IMPRINT",FACE,{"disambiguationData":[TD([[makeQuery(id+"F0.imprint","IMPRINT",EDGE,{"derivedFrom":sQuery(id+"F0.wireOp",EDGE,"E45")}),1.0]])]});
            var Q131;
            Q131=makeQuery(id+"F0.imprint","IMPRINT",FACE,{"disambiguationData":[TD([[makeQuery(id+"F0.imprint","IMPRINT",EDGE,{"derivedFrom":sQuery(id+"F0.wireOp",EDGE,"E141")}),1.0]])]});
            var Q132;
            Q132=makeQuery(id+"F0.imprint","IMPRINT",FACE,{"disambiguationData":[TD([[makeQuery(id+"F0.imprint","IMPRINT",EDGE,{"derivedFrom":sQuery(id+"F0.wireOp",EDGE,"E77")}),1.0]])]});
            var Q133;
            Q133=makeQuery(id+"F0.imprint","IMPRINT",FACE,{"disambiguationData":[TD([[makeQuery(id+"F0.imprint","IMPRINT",EDGE,{"derivedFrom":sQuery(id+"F0.wireOp",EDGE,"E32")}),1.0]])]});
            var Q134;
            Q134=makeQuery(id+"F0.imprint","IMPRINT",FACE,{"disambiguationData":[TD([[makeQuery(id+"F0.imprint","IMPRINT",EDGE,{"derivedFrom":sQuery(id+"F0.wireOp",EDGE,"E93")}),1.0]])]});
            var Q135;
            Q135=makeQuery(id+"F0.imprint","IMPRINT",FACE,{"disambiguationData":[TD([[makeQuery(id+"F0.imprint","IMPRINT",EDGE,{"derivedFrom":sQuery(id+"F0.wireOp",EDGE,"E127")}),1.0]])]});
            var Q136;
            Q136=makeQuery(id+"F0.imprint","IMPRINT",FACE,{"disambiguationData":[TD([[makeQuery(id+"F0.imprint","IMPRINT",EDGE,{"derivedFrom":sQuery(id+"F0.wireOp",EDGE,"E42")}),1.0]])]});
            var Q137;
            Q137=makeQuery(id+"F0.imprint","IMPRINT",FACE,{"disambiguationData":[TD([[makeQuery(id+"F0.imprint","IMPRINT",EDGE,{"derivedFrom":sQuery(id+"F0.wireOp",EDGE,"E58")}),1.0]])]});
            var Q138;
            Q138=makeQuery(id+"F0.imprint","IMPRINT",FACE,{"disambiguationData":[TD([[makeQuery(id+"F0.imprint","IMPRINT",EDGE,{"derivedFrom":sQuery(id+"F0.wireOp",EDGE,"E159")}),1.0]])]});
            var Q139;
            Q139=makeQuery(id+"F0.imprint","IMPRINT",FACE,{"disambiguationData":[TD([[makeQuery(id+"F0.imprint","IMPRINT",EDGE,{"derivedFrom":sQuery(id+"F0.wireOp",EDGE,"E128")}),1.0]])]});
            var Q140;
            Q140=makeQuery(id+"F0.imprint","IMPRINT",FACE,{"disambiguationData":[TD([[makeQuery(id+"F0.imprint","IMPRINT",EDGE,{"derivedFrom":sQuery(id+"F0.wireOp",EDGE,"E122")}),1.0]])]});
            var Q141;
            Q141=makeQuery(id+"F0.imprint","IMPRINT",FACE,{"disambiguationData":[TD([[makeQuery(id+"F0.imprint","IMPRINT",EDGE,{"derivedFrom":sQuery(id+"F0.wireOp",EDGE,"E96")}),1.0]])]});
            var Q142;
            Q142=makeQuery(id+"F0.imprint","IMPRINT",FACE,{"disambiguationData":[TD([[makeQuery(id+"F0.imprint","IMPRINT",EDGE,{"derivedFrom":sQuery(id+"F0.wireOp",EDGE,"E80")}),1.0]])]});
            var Q143;
            Q143=makeQuery(id+"F0.imprint","IMPRINT",FACE,{"disambiguationData":[TD([[makeQuery(id+"F0.imprint","IMPRINT",EDGE,{"derivedFrom":sQuery(id+"F0.wireOp",EDGE,"E106")}),1.0]])]});
            var Q144;
            Q144=makeQuery(id+"F0.imprint","IMPRINT",FACE,{"disambiguationData":[TD([[makeQuery(id+"F0.imprint","IMPRINT",EDGE,{"derivedFrom":sQuery(id+"F0.wireOp",EDGE,"E79")}),1.0]])]});
            var Q145;
            Q145=makeQuery(id+"F0.imprint","IMPRINT",FACE,{"disambiguationData":[TD([[makeQuery(id+"F0.imprint","IMPRINT",EDGE,{"derivedFrom":sQuery(id+"F0.wireOp",EDGE,"E95")}),1.0]])]});
            var Q146;
            Q146=makeQuery(id+"F0.imprint","IMPRINT",FACE,{"disambiguationData":[TD([[makeQuery(id+"F0.imprint","IMPRINT",EDGE,{"derivedFrom":sQuery(id+"F0.wireOp",EDGE,"E111")}),1.0]])]});
            var Q147;
            Q147=makeQuery(id+"F0.imprint","IMPRINT",FACE,{"disambiguationData":[TD([[makeQuery(id+"F0.imprint","IMPRINT",EDGE,{"derivedFrom":sQuery(id+"F0.wireOp",EDGE,"E31")}),1.0]])]});
            var Q148;
            Q148=makeQuery(id+"F0.imprint","IMPRINT",FACE,{"disambiguationData":[TD([[makeQuery(id+"F0.imprint","IMPRINT",EDGE,{"derivedFrom":sQuery(id+"F0.wireOp",EDGE,"E47")}),1.0]])]});
            var Q149;
            Q149=makeQuery(id+"F0.imprint","IMPRINT",FACE,{"disambiguationData":[TD([[makeQuery(id+"F0.imprint","IMPRINT",EDGE,{"derivedFrom":sQuery(id+"F0.wireOp",EDGE,"E108")}),1.0]])]});
            var Q150;
            Q150=makeQuery(id+"F0.imprint","IMPRINT",FACE,{"disambiguationData":[TD([[makeQuery(id+"F0.imprint","IMPRINT",EDGE,{"derivedFrom":sQuery(id+"F0.wireOp",EDGE,"E124")}),1.0]])]});
            var Q151;
            Q151=makeQuery(id+"F0.imprint","IMPRINT",FACE,{"disambiguationData":[TD([[makeQuery(id+"F0.imprint","IMPRINT",EDGE,{"derivedFrom":sQuery(id+"F0.wireOp",EDGE,"E156")}),1.0]])]});
            var Q152;
            Q152=makeQuery(id+"F0.imprint","IMPRINT",FACE,{"disambiguationData":[TD([[makeQuery(id+"F0.imprint","IMPRINT",EDGE,{"derivedFrom":sQuery(id+"F0.wireOp",EDGE,"E91")}),1.0]])]});
            var Q153;
            Q153=makeQuery(id+"F0.imprint","IMPRINT",FACE,{"disambiguationData":[TD([[makeQuery(id+"F0.imprint","IMPRINT",EDGE,{"derivedFrom":sQuery(id+"F0.wireOp",EDGE,"E44")}),1.0]])]});
            var Q154;
            Q154=makeQuery(id+"F0.imprint","IMPRINT",FACE,{"disambiguationData":[TD([[makeQuery(id+"F0.imprint","IMPRINT",EDGE,{"derivedFrom":sQuery(id+"F0.wireOp",EDGE,"E76")}),1.0]])]});
            var Q155;
            Q155=makeQuery(id+"F0.imprint","IMPRINT",FACE,{"disambiguationData":[TD([[makeQuery(id+"F0.imprint","IMPRINT",EDGE,{"derivedFrom":sQuery(id+"F0.wireOp",EDGE,"E59")}),1.0]])]});
            var Q156;
            Q156=makeQuery(id+"F0.imprint","IMPRINT",FACE,{"disambiguationData":[TD([[makeQuery(id+"F0.imprint","IMPRINT",EDGE,{"derivedFrom":sQuery(id+"F0.wireOp",EDGE,"E92")}),1.0]])]});
            var Q157;
            Q157=makeQuery(id+"F0.imprint","IMPRINT",FACE,{"disambiguationData":[TD([[makeQuery(id+"F0.imprint","IMPRINT",EDGE,{"derivedFrom":sQuery(id+"F0.wireOp",EDGE,"E28")}),1.0]])]});
            var Q158;
            Q158=makeQuery(id+"F0.imprint","IMPRINT",FACE,{"disambiguationData":[TD([[makeQuery(id+"F0.imprint","IMPRINT",EDGE,{"derivedFrom":sQuery(id+"F0.wireOp",EDGE,"E139")}),1.0]])]});
            var Q159;
            Q159=makeQuery(id+"F0.imprint","IMPRINT",FACE,{"disambiguationData":[TD([[makeQuery(id+"F0.imprint","IMPRINT",EDGE,{"derivedFrom":sQuery(id+"F0.wireOp",EDGE,"E126")}),1.0]])]});
            var Q160;
            Q160=makeQuery(id+"F0.imprint","IMPRINT",FACE,{"disambiguationData":[TD([[makeQuery(id+"F0.imprint","IMPRINT",EDGE,{"derivedFrom":sQuery(id+"F0.wireOp",EDGE,"E142")}),1.0]])]});
            var Q161;
            Q161=makeQuery(id+"F0.imprint","IMPRINT",FACE,{"disambiguationData":[TD([[makeQuery(id+"F0.imprint","IMPRINT",EDGE,{"derivedFrom":sQuery(id+"F0.wireOp",EDGE,"E62")}),1.0]])]});
            var Q162;
            Q162=makeQuery(id+"F0.imprint","IMPRINT",FACE,{"disambiguationData":[TD([[makeQuery(id+"F0.imprint","IMPRINT",EDGE,{"derivedFrom":sQuery(id+"F0.wireOp",EDGE,"E110")}),1.0]])]});
            var Q163;
            Q163=makeQuery(id+"F0.imprint","IMPRINT",FACE,{"disambiguationData":[TD([[makeQuery(id+"F0.imprint","IMPRINT",EDGE,{"derivedFrom":sQuery(id+"F0.wireOp",EDGE,"E30")}),1.0]])]});
            var Q164;
            Q164=makeQuery(id+"F0.imprint","IMPRINT",FACE,{"disambiguationData":[TD([[makeQuery(id+"F0.imprint","IMPRINT",EDGE,{"derivedFrom":sQuery(id+"F0.wireOp",EDGE,"E63")}),1.0]])]});
            var Q165;
            Q165=sQuery(id+"F0.wireOp",EDGE,"E32");
            var Q166;
            Q166=sQuery(id+"F0.wireOp",EDGE,"E33");
            var Q167;
            Q167=sQuery(id+"F0.wireOp",EDGE,"E5");
            var Q168;
            Q168=sQuery(id+"F0.wireOp",EDGE,"E6");
            var Q169;
            Q169=sQuery(id+"F0.wireOp",EDGE,"E128");
            var Q170;
            Q170=sQuery(id+"F0.wireOp",EDGE,"E160");
            var Q171;
            Q171=sQuery(id+"F0.wireOp",EDGE,"E144");
            var Q172;
            Q172=sQuery(id+"F0.wireOp",EDGE,"E154");
            var Q173;
            Q173=sQuery(id+"F0.wireOp",EDGE,"E90");
            var Q174;
            Q174=sQuery(id+"F0.wireOp",EDGE,"E159");
            var Q175;
            Q175=sQuery(id+"F0.wireOp",EDGE,"E4");
            var Q176;
            Q176=sQuery(id+"F0.wireOp",EDGE,"E3");
            var Q177;
            Q177=sQuery(id+"F0.wireOp",EDGE,"E2");
            var Q178;
            Q178=sQuery(id+"F0.wireOp",EDGE,"E1");
            var Q179;
            Q179=sQuery(id+"F0.wireOp",EDGE,"E63");
            var Q180;
            Q180=sQuery(id+"F0.wireOp",EDGE,"E0");
            var Q181;
            Q181=sQuery(id+"F0.wireOp",EDGE,"E129");
            var Q182;
            Q182=sQuery(id+"F0.wireOp",EDGE,"E161");
            var Q183;
            Q183=sQuery(id+"F0.wireOp",EDGE,"E145");
            var Q184;
            Q184=sQuery(id+"F0.wireOp",EDGE,"E15");
            var Q185;
            Q185=sQuery(id+"F0.wireOp",EDGE,"E13");
            var Q186;
            Q186=sQuery(id+"F0.wireOp",EDGE,"E143");
            var Q187;
            Q187=sQuery(id+"F0.wireOp",EDGE,"E127");
            var Q188;
            Q188=sQuery(id+"F0.wireOp",EDGE,"E64");
            var Q189;
            Q189=sQuery(id+"F0.wireOp",EDGE,"E106");
            var Q190;
            Q190=sQuery(id+"F0.wireOp",EDGE,"E122");
            var Q191;
            Q191=sQuery(id+"F0.wireOp",EDGE,"E138");
            var Q192;
            Q192=sQuery(id+"F0.wireOp",EDGE,"E95");
            var Q193;
            Q193=sQuery(id+"F0.wireOp",EDGE,"E58");
            var Q194;
            Q194=sQuery(id+"F0.wireOp",EDGE,"E42");
            var Q195;
            Q195=sQuery(id+"F0.wireOp",EDGE,"E16");
            var Q196;
            Q196=sQuery(id+"F0.wireOp",EDGE,"E74");
            var Q197;
            Q197=sQuery(id+"F0.wireOp",EDGE,"E48");
            var Q198;
            Q198=sQuery(id+"F0.wireOp",EDGE,"E121");
            var Q199;
            Q199=sQuery(id+"F0.wireOp",EDGE,"E79");
            var Q200;
            Q200=sQuery(id+"F0.wireOp",EDGE,"E47");
            var Q201;
            Q201=sQuery(id+"F0.wireOp",EDGE,"E111");
            var Q202;
            Q202=sQuery(id+"F0.wireOp",EDGE,"E26");
            var Q203;
            Q203=sQuery(id+"F0.wireOp",EDGE,"E7");
            var Q204;
            Q204=sQuery(id+"F0.wireOp",EDGE,"E80");
            var Q205;
            Q205=sQuery(id+"F0.wireOp",EDGE,"E8");
            var Q206;
            Q206=sQuery(id+"F0.wireOp",EDGE,"E105");
            var Q207;
            Q207=sQuery(id+"F0.wireOp",EDGE,"E137");
            var Q208;
            Q208=sQuery(id+"F0.wireOp",EDGE,"E41");
            var Q209;
            Q209=sQuery(id+"F0.wireOp",EDGE,"E153");
            var Q210;
            Q210=sQuery(id+"F0.wireOp",EDGE,"E57");
            var Q211;
            Q211=sQuery(id+"F0.wireOp",EDGE,"E96");
            var Q212;
            Q212=sQuery(id+"F0.wireOp",EDGE,"E73");
            var Q213;
            Q213=sQuery(id+"F0.wireOp",EDGE,"E112");
            var Q214;
            Q214=sQuery(id+"F0.wireOp",EDGE,"E89");
            var Q215;
            Q215=sQuery(id+"F0.wireOp",EDGE,"E126");
            var Q216;
            Q216=sQuery(id+"F0.wireOp",EDGE,"E25");
            var Q217;
            Q217=sQuery(id+"F0.wireOp",EDGE,"E142");
            var Q218;
            Q218=sQuery(id+"F0.wireOp",EDGE,"E62");
            var Q219;
            Q219=sQuery(id+"F0.wireOp",EDGE,"E158");
            var Q220;
            Q220=sQuery(id+"F0.wireOp",EDGE,"E78");
            var Q221;
            Q221=sQuery(id+"F0.wireOp",EDGE,"E94");
            var Q222;
            Q222=sQuery(id+"F0.wireOp",EDGE,"E110");
            var Q223;
            Q223=sQuery(id+"F0.wireOp",EDGE,"E30");
            var Q224;
            Q224=sQuery(id+"F0.wireOp",EDGE,"E108");
            var Q225;
            Q225=sQuery(id+"F0.wireOp",EDGE,"E46");
            var Q226;
            Q226=sQuery(id+"F0.wireOp",EDGE,"E37");
            var Q227;
            Q227=sQuery(id+"F0.wireOp",EDGE,"E140");
            var Q228;
            Q228=sQuery(id+"F0.wireOp",EDGE,"E156");
            var Q229;
            Q229=sQuery(id+"F0.wireOp",EDGE,"E124");
            var Q230;
            Q230=sQuery(id+"F0.wireOp",EDGE,"E44");
            var Q231;
            Q231=sQuery(id+"F0.wireOp",EDGE,"E76");
            var Q232;
            Q232=sQuery(id+"F0.wireOp",EDGE,"E104");
            var Q233;
            Q233=sQuery(id+"F0.wireOp",EDGE,"E92");
            var Q234;
            Q234=sQuery(id+"F0.wireOp",EDGE,"E28");
            var Q235;
            Q235=sQuery(id+"F0.wireOp",EDGE,"E152");
            var Q236;
            Q236=sQuery(id+"F0.wireOp",EDGE,"E10");
            var Q237;
            Q237=sQuery(id+"F0.wireOp",EDGE,"E136");
            var Q238;
            Q238=sQuery(id+"F0.wireOp",EDGE,"E49");
            var Q239;
            Q239=sQuery(id+"F0.wireOp",EDGE,"E56");
            var Q240;
            Q240=sQuery(id+"F0.wireOp",EDGE,"E40");
            var Q241;
            Q241=sQuery(id+"F0.wireOp",EDGE,"E72");
            var Q242;
            Q242=sQuery(id+"F0.wireOp",EDGE,"E12");
            var Q243;
            Q243=sQuery(id+"F0.wireOp",EDGE,"E17");
            var Q244;
            Q244=sQuery(id+"F0.wireOp",EDGE,"E103");
            var Q245;
            Q245=sQuery(id+"F0.wireOp",EDGE,"E135");
            var Q246;
            Q246=sQuery(id+"F0.wireOp",EDGE,"E119");
            var Q247;
            Q247=sQuery(id+"F0.wireOp",EDGE,"E113");
            var Q248;
            Q248=sQuery(id+"F0.wireOp",EDGE,"E151");
            var Q249;
            Q249=sQuery(id+"F0.wireOp",EDGE,"E91");
            var Q250;
            Q250=sQuery(id+"F0.wireOp",EDGE,"E59");
            var Q251;
            Q251=sQuery(id+"F0.wireOp",EDGE,"E43");
            var Q252;
            Q252=sQuery(id+"F0.wireOp",EDGE,"E75");
            var Q253;
            Q253=sQuery(id+"F0.wireOp",EDGE,"E81");
            var Q254;
            Q254=sQuery(id+"F0.wireOp",EDGE,"E155");
            var Q255;
            Q255=sQuery(id+"F0.wireOp",EDGE,"E139");
            var Q256;
            Q256=sQuery(id+"F0.wireOp",EDGE,"E65");
            var Q257;
            Q257=sQuery(id+"F0.wireOp",EDGE,"E123");
            var Q258;
            Q258=sQuery(id+"F0.wireOp",EDGE,"E45");
            var Q259;
            Q259=sQuery(id+"F0.wireOp",EDGE,"E125");
            var Q260;
            Q260=sQuery(id+"F0.wireOp",EDGE,"E141");
            var Q261;
            Q261=sQuery(id+"F0.wireOp",EDGE,"E157");
            var Q262;
            Q262=sQuery(id+"F0.wireOp",EDGE,"E61");
            var Q263;
            Q263=sQuery(id+"F0.wireOp",EDGE,"E77");
            var Q264;
            Q264=sQuery(id+"F0.wireOp",EDGE,"E107");
            var Q265;
            Q265=sQuery(id+"F0.wireOp",EDGE,"E93");
            var Q266;
            Q266=sQuery(id+"F0.wireOp",EDGE,"E109");
            var Q267;
            Q267=sQuery(id+"F0.wireOp",EDGE,"E55");
            var Q268;
            Q268=sQuery(id+"F0.wireOp",EDGE,"E71");
            var Q269;
            Q269=sQuery(id+"F0.wireOp",EDGE,"E87");
            var Q270;
            Q270=sQuery(id+"F0.wireOp",EDGE,"E134");
            var Q271;
            Q271=sQuery(id+"F0.wireOp",EDGE,"E70");
            var Q272;
            Q272=sQuery(id+"F0.wireOp",EDGE,"E86");
            var Q273;
            Q273=sQuery(id+"F0.wireOp",EDGE,"E102");
            var Q274;
            Q274=sQuery(id+"F0.wireOp",EDGE,"E118");
            var Q275;
            Q275=sQuery(id+"F0.wireOp",EDGE,"E50");
            var Q276;
            Q276=sQuery(id+"F0.wireOp",EDGE,"E149");
            var Q277;
            Q277=sQuery(id+"F0.wireOp",EDGE,"E133");
            var Q278;
            Q278=sQuery(id+"F0.wireOp",EDGE,"E165");
            var Q279;
            Q279=sQuery(id+"F0.wireOp",EDGE,"E117");
            var Q280;
            Q280=sQuery(id+"F0.wireOp",EDGE,"E18");
            var Q281;
            Q281=sQuery(id+"F0.wireOp",EDGE,"E53");
            var Q282;
            Q282=sQuery(id+"F0.wireOp",EDGE,"E114");
            var Q283;
            Q283=sQuery(id+"F0.wireOp",EDGE,"E98");
            var Q284;
            Q284=sQuery(id+"F0.wireOp",EDGE,"E82");
            var Q285;
            Q285=sQuery(id+"F0.wireOp",EDGE,"E66");
            var Q286;
            Q286=sQuery(id+"F0.wireOp",EDGE,"E162");
            var Q287;
            Q287=sQuery(id+"F0.wireOp",EDGE,"E130");
            var Q288;
            Q288=sQuery(id+"F0.wireOp",EDGE,"E132");
            var Q289;
            Q289=sQuery(id+"F0.wireOp",EDGE,"E148");
            var Q290;
            Q290=sQuery(id+"F0.wireOp",EDGE,"E164");
            var Q291;
            Q291=sQuery(id+"F0.wireOp",EDGE,"E68");
            var Q292;
            Q292=sQuery(id+"F0.wireOp",EDGE,"E100");
            var Q293;
            Q293=sQuery(id+"F0.wireOp",EDGE,"E116");
            var Q294;
            Q294=sQuery(id+"F0.wireOp",EDGE,"E51");
            var Q295;
            Q295=sQuery(id+"F0.wireOp",EDGE,"E36");
            var Q296;
            Q296=sQuery(id+"F0.wireOp",EDGE,"E115");
            var Q297;
            Q297=sQuery(id+"F0.wireOp",EDGE,"E52");
            var Q298;
            Q298=sQuery(id+"F0.wireOp",EDGE,"E99");
            var Q299;
            Q299=sQuery(id+"F0.wireOp",EDGE,"E83");
            var Q300;
            Q300=sQuery(id+"F0.wireOp",EDGE,"E67");
            var Q301;
            Q301=sQuery(id+"F0.wireOp",EDGE,"E163");
            var Q302;
            Q302=sQuery(id+"F0.wireOp",EDGE,"E131");
            var Q303;
            Q303=sQuery(id+"F0.wireOp",EDGE,"E14");
            var Q304;
            Q304=sQuery(id+"F0.wireOp",EDGE,"E31");
            var Q305;
            Q305=sQuery(id+"F0.wireOp",EDGE,"E9");
            var Q306;
            Q306=sQuery(id+"F0.wireOp",EDGE,"E60");
            var Q307;
            Q307=sQuery(id+"F0.wireOp",EDGE,"E120");
            var Q308;
            Q308=sQuery(id+"F0.wireOp",EDGE,"E11");
            var Q309;
            Q309=sQuery(id+"F0.wireOp",EDGE,"E88");
            var Q310;
            Q310=sQuery(id+"F0.wireOp",EDGE,"E24");
            var Q311;
            Q311=sQuery(id+"F0.wireOp",EDGE,"E97");
            var Q312;
            Q312=sQuery(id+"F0.wireOp",EDGE,"E27");
            var Q313;
            Q313=sQuery(id+"F0.wireOp",EDGE,"E29");
            var Q314;
            Q314=sQuery(id+"F0.wireOp",EDGE,"E39");
            var Q315;
            Q315=sQuery(id+"F0.wireOp",EDGE,"E23");
            var Q316;
            Q316=sQuery(id+"F0.wireOp",EDGE,"E150");
            var Q317;
            Q317=sQuery(id+"F0.wireOp",EDGE,"E22");
            var Q318;
            Q318=sQuery(id+"F0.wireOp",EDGE,"E38");
            var Q319;
            Q319=sQuery(id+"F0.wireOp",EDGE,"E54");
            var Q320;
            Q320=sQuery(id+"F0.wireOp",EDGE,"E69");
            var Q321;
            Q321=sQuery(id+"F0.wireOp",EDGE,"E85");
            var Q322;
            Q322=sQuery(id+"F0.wireOp",EDGE,"E101");
            var Q323;
            Q323=sQuery(id+"F0.wireOp",EDGE,"E21");
            var Q324;
            Q324=sQuery(id+"F0.wireOp",EDGE,"E34");
            var Q325;
            Q325=sQuery(id+"F0.wireOp",EDGE,"E146");
            var Q326;
            Q326=sQuery(id+"F0.wireOp",EDGE,"E84");
            var Q327;
            Q327=sQuery(id+"F0.wireOp",EDGE,"E35");
            var Q328;
            Q328=sQuery(id+"F0.wireOp",EDGE,"E147");
            var Q329;
            Q329=sQuery(id+"F0.wireOp",EDGE,"E20");
            extrude(context, id + "F1", {"entities" : qUnion([Q0, Q1, Q2, Q3, Q4, Q5, Q6, Q7, Q8, Q9, Q10, Q11, Q12, Q13, Q14, Q15, Q16, Q17, Q18, Q19, Q20, Q21, Q22, Q23, Q24, Q25, Q26, Q27, Q28, Q29, Q30, Q31, Q32, Q33, Q34, Q35, Q36, Q37, Q38, Q39, Q40, Q41, Q42, Q43, Q44, Q45, Q46, Q47, Q48, Q49, Q50, Q51, Q52, Q53, Q54, Q55, Q56, Q57, Q58, Q59, Q60, Q61, Q62, Q63, Q64, Q65, Q66, Q67, Q68, Q69, Q70, Q71, Q72, Q73, Q74, Q75, Q76, Q77, Q78, Q79, Q80, Q81, Q82, Q83, Q84, Q85, Q86, Q87, Q88, Q89, Q90, Q91, Q92, Q93, Q94, Q95, Q96, Q97, Q98, Q99, Q100, Q101, Q102, Q103, Q104, Q105, Q106, Q107, Q108, Q109, Q110, Q111, Q112, Q113, Q114, Q115, Q116, Q117, Q118, Q119, Q120, Q121, Q122, Q123, Q124, Q125, Q126, Q127, Q128, Q129, Q130, Q131, Q132, Q133, Q134, Q135, Q136, Q137, Q138, Q139, Q140, Q141, Q142, Q143, Q144, Q145, Q146, Q147, Q148, Q149, Q150, Q151, Q152, Q153, Q154, Q155, Q156, Q157, Q158, Q159, Q160, Q161, Q162, Q163, Q164]), "surfaceEntities" : qUnion([Q165, Q166, Q167, Q168, Q169, Q170, Q171, Q172, Q173, Q174, Q175, Q176, Q177, Q178, Q179, Q180, Q181, Q182, Q183, Q184, Q185, Q186, Q187, Q188, Q189, Q190, Q191, Q192, Q193, Q194, Q195, Q196, Q197, Q198, Q199, Q200, Q201, Q202, Q203, Q204, Q205, Q206, Q207, Q208, Q209, Q210, Q211, Q212, Q213, Q214, Q215, Q216, Q217, Q218, Q219, Q220, Q221, Q222, Q223, Q224, Q225, Q226, Q227, Q228, Q229, Q230, Q231, Q232, Q233, Q234, Q235, Q236, Q237, Q238, Q239, Q240, Q241, Q242, Q243, Q244, Q245, Q246, Q247, Q248, Q249, Q250, Q251, Q252, Q253, Q254, Q255, Q256, Q257, Q258, Q259, Q260, Q261, Q262, Q263, Q264, Q265, Q266, Q267, Q268, Q269, Q270, Q271, Q272, Q273, Q274, Q275, Q276, Q277, Q278, Q279, Q280, Q281, Q282, Q283, Q284, Q285, Q286, Q287, Q288, Q289, Q290, Q291, Q292, Q293, Q294, Q295, Q296, Q297, Q298, Q299, Q300, Q301, Q302, Q303, Q304, Q305, Q306, Q307, Q308, Q309, Q310, Q311, Q312, Q313, Q314, Q315, Q316, Q317, Q318, Q319, Q320, Q321, Q322, Q323, Q324, Q325, Q326, Q327, Q328, Q329]), "depth" : 1.2 * mm});
        }
        {
            var Q0;
            Q0=makeQuery(id+"F1.opExtrude","CAP_FACE",FACE,{"disambiguationData":[OSD([sQuery(id+"F0.wireOp",EDGE,"E76")])],"isStart":false});
            var Q1;
            Q1=makeQuery(id+"F1.opExtrude","CAP_EDGE",EDGE,{"disambiguationData":[OSD([sQuery(id+"F0.wireOp",EDGE,"E75")])],"isStart":false});
            var Q2;
            Q2=makeQuery(id+"F1.opExtrude","CAP_EDGE",EDGE,{"disambiguationData":[OSD([sQuery(id+"F0.wireOp",EDGE,"E77")])],"isStart":false});
            var Q3;
            Q3=makeQuery(id+"F1.opExtrude","CAP_EDGE",EDGE,{"disambiguationData":[OSD([sQuery(id+"F0.wireOp",EDGE,"E74")])],"isStart":false});
            var Q4;
            Q4=makeQuery(id+"F1.opExtrude","CAP_EDGE",EDGE,{"disambiguationData":[OSD([sQuery(id+"F0.wireOp",EDGE,"E73")])],"isStart":false});
            var Q5;
            Q5=makeQuery(id+"F1.opExtrude","CAP_EDGE",EDGE,{"disambiguationData":[OSD([sQuery(id+"F0.wireOp",EDGE,"E135")])],"isStart":false});
            var Q6;
            Q6=makeQuery(id+"F1.opExtrude","CAP_EDGE",EDGE,{"disambiguationData":[OSD([sQuery(id+"F0.wireOp",EDGE,"E136")])],"isStart":false});
            var Q7;
            Q7=makeQuery(id+"F1.opExtrude","CAP_EDGE",EDGE,{"disambiguationData":[OSD([sQuery(id+"F0.wireOp",EDGE,"E137")])],"isStart":false});
            var Q8;
            Q8=makeQuery(id+"F1.opExtrude","CAP_EDGE",EDGE,{"disambiguationData":[OSD([sQuery(id+"F0.wireOp",EDGE,"E138")])],"isStart":false});
            var Q9;
            Q9=makeQuery(id+"F1.opExtrude","CAP_EDGE",EDGE,{"disambiguationData":[OSD([sQuery(id+"F0.wireOp",EDGE,"E139")])],"isStart":false});
            var Q10;
            Q10=makeQuery(id+"F1.opExtrude","CAP_EDGE",EDGE,{"disambiguationData":[OSD([sQuery(id+"F0.wireOp",EDGE,"E140")])],"isStart":false});
            var Q11;
            Q11=makeQuery(id+"F1.opExtrude","CAP_EDGE",EDGE,{"disambiguationData":[OSD([sQuery(id+"F0.wireOp",EDGE,"E141")])],"isStart":false});
            var Q12;
            Q12=makeQuery(id+"F1.opExtrude","CAP_EDGE",EDGE,{"disambiguationData":[OSD([sQuery(id+"F0.wireOp",EDGE,"E142")])],"isStart":false});
            var Q13;
            Q13=makeQuery(id+"F1.opExtrude","CAP_EDGE",EDGE,{"disambiguationData":[OSD([sQuery(id+"F0.wireOp",EDGE,"E79")])],"isStart":false});
            var Q14;
            Q14=makeQuery(id+"F1.opExtrude","CAP_EDGE",EDGE,{"disambiguationData":[OSD([sQuery(id+"F0.wireOp",EDGE,"E78")])],"isStart":false});
            var Q15;
            Q15=makeQuery(id+"F1.opExtrude","CAP_EDGE",EDGE,{"disambiguationData":[OSD([sQuery(id+"F0.wireOp",EDGE,"E80")])],"isStart":false});
            var Q16;
            Q16=makeQuery(id+"F1.opExtrude","CAP_EDGE",EDGE,{"disambiguationData":[OSD([sQuery(id+"F0.wireOp",EDGE,"E11")])],"isStart":false});
            var Q17;
            Q17=makeQuery(id+"F1.opExtrude","CAP_EDGE",EDGE,{"disambiguationData":[OSD([sQuery(id+"F0.wireOp",EDGE,"E10")])],"isStart":false});
            var Q18;
            Q18=makeQuery(id+"F1.opExtrude","CAP_EDGE",EDGE,{"disambiguationData":[OSD([sQuery(id+"F0.wireOp",EDGE,"E9")])],"isStart":false});
            var Q19;
            Q19=makeQuery(id+"F1.opExtrude","CAP_EDGE",EDGE,{"disambiguationData":[OSD([sQuery(id+"F0.wireOp",EDGE,"E8")])],"isStart":false});
            var Q20;
            Q20=makeQuery(id+"F1.opExtrude","CAP_EDGE",EDGE,{"disambiguationData":[OSD([sQuery(id+"F0.wireOp",EDGE,"E7")])],"isStart":false});
            var Q21;
            Q21=makeQuery(id+"F1.opExtrude","CAP_EDGE",EDGE,{"disambiguationData":[OSD([sQuery(id+"F0.wireOp",EDGE,"E5")])],"isStart":false});
            var Q22;
            Q22=makeQuery(id+"F1.opExtrude","CAP_EDGE",EDGE,{"disambiguationData":[OSD([sQuery(id+"F0.wireOp",EDGE,"E4")])],"isStart":false});
            var Q23;
            Q23=makeQuery(id+"F1.opExtrude","CAP_EDGE",EDGE,{"disambiguationData":[OSD([sQuery(id+"F0.wireOp",EDGE,"E6")])],"isStart":false});
            var Q24;
            Q24=makeQuery(id+"F1.opExtrude","CAP_EDGE",EDGE,{"disambiguationData":[OSD([sQuery(id+"F0.wireOp",EDGE,"E3")])],"isStart":false});
            var Q25;
            Q25=makeQuery(id+"F1.opExtrude","CAP_EDGE",EDGE,{"disambiguationData":[OSD([sQuery(id+"F0.wireOp",EDGE,"E71")])],"isStart":false});
            var Q26;
            Q26=makeQuery(id+"F1.opExtrude","CAP_EDGE",EDGE,{"disambiguationData":[OSD([sQuery(id+"F0.wireOp",EDGE,"E72")])],"isStart":false});
            var Q27;
            Q27=makeQuery(id+"F1.opExtrude","CAP_EDGE",EDGE,{"disambiguationData":[OSD([sQuery(id+"F0.wireOp",EDGE,"E69")])],"isStart":false});
            var Q28;
            Q28=makeQuery(id+"F1.opExtrude","CAP_EDGE",EDGE,{"disambiguationData":[OSD([sQuery(id+"F0.wireOp",EDGE,"E70")])],"isStart":false});
            var Q29;
            Q29=makeQuery(id+"F1.opExtrude","CAP_EDGE",EDGE,{"disambiguationData":[OSD([sQuery(id+"F0.wireOp",EDGE,"E134")])],"isStart":false});
            var Q30;
            Q30=makeQuery(id+"F1.opExtrude","CAP_EDGE",EDGE,{"disambiguationData":[OSD([sQuery(id+"F0.wireOp",EDGE,"E133")])],"isStart":false});
            var Q31;
            Q31=makeQuery(id+"F1.opExtrude","CAP_EDGE",EDGE,{"disambiguationData":[OSD([sQuery(id+"F0.wireOp",EDGE,"E131")])],"isStart":false});
            var Q32;
            Q32=makeQuery(id+"F1.opExtrude","CAP_EDGE",EDGE,{"disambiguationData":[OSD([sQuery(id+"F0.wireOp",EDGE,"E132")])],"isStart":false});
            var Q33;
            Q33=makeQuery(id+"F1.opExtrude","CAP_EDGE",EDGE,{"disambiguationData":[OSD([sQuery(id+"F0.wireOp",EDGE,"E68")])],"isStart":false});
            var Q34;
            Q34=makeQuery(id+"F1.opExtrude","CAP_EDGE",EDGE,{"disambiguationData":[OSD([sQuery(id+"F0.wireOp",EDGE,"E1")])],"isStart":false});
            var Q35;
            Q35=makeQuery(id+"F1.opExtrude","CAP_EDGE",EDGE,{"disambiguationData":[OSD([sQuery(id+"F0.wireOp",EDGE,"E2")])],"isStart":false});
            var Q36;
            Q36=makeQuery(id+"F1.opExtrude","CAP_EDGE",EDGE,{"disambiguationData":[OSD([sQuery(id+"F0.wireOp",EDGE,"E14")])],"isStart":false});
            var Q37;
            Q37=makeQuery(id+"F1.opExtrude","CAP_EDGE",EDGE,{"disambiguationData":[OSD([sQuery(id+"F0.wireOp",EDGE,"E13")])],"isStart":false});
            var Q38;
            Q38=makeQuery(id+"F1.opExtrude","CAP_EDGE",EDGE,{"disambiguationData":[OSD([sQuery(id+"F0.wireOp",EDGE,"E12")])],"isStart":false});
            var Q39;
            Q39=makeQuery(id+"F1.opExtrude","CAP_EDGE",EDGE,{"disambiguationData":[OSD([sQuery(id+"F0.wireOp",EDGE,"E15")])],"isStart":false});
            var Q40;
            Q40=makeQuery(id+"F1.opExtrude","CAP_EDGE",EDGE,{"disambiguationData":[OSD([sQuery(id+"F0.wireOp",EDGE,"E16")])],"isStart":false});
            var Q41;
            Q41=makeQuery(id+"F1.opExtrude","CAP_EDGE",EDGE,{"disambiguationData":[OSD([sQuery(id+"F0.wireOp",EDGE,"E17")])],"isStart":false});
            var Q42;
            Q42=makeQuery(id+"F1.opExtrude","CAP_EDGE",EDGE,{"disambiguationData":[OSD([sQuery(id+"F0.wireOp",EDGE,"E18")])],"isStart":false});
            var Q43;
            Q43=makeQuery(id+"F1.opExtrude","CAP_EDGE",EDGE,{"disambiguationData":[OSD([sQuery(id+"F0.wireOp",EDGE,"E81")])],"isStart":false});
            var Q44;
            Q44=makeQuery(id+"F1.opExtrude","CAP_EDGE",EDGE,{"disambiguationData":[OSD([sQuery(id+"F0.wireOp",EDGE,"E82")])],"isStart":false});
            var Q45;
            Q45=makeQuery(id+"F1.opExtrude","CAP_EDGE",EDGE,{"disambiguationData":[OSD([sQuery(id+"F0.wireOp",EDGE,"E83")])],"isStart":false});
            var Q46;
            Q46=makeQuery(id+"F1.opExtrude","CAP_EDGE",EDGE,{"disambiguationData":[OSD([sQuery(id+"F0.wireOp",EDGE,"E143")])],"isStart":false});
            var Q47;
            Q47=makeQuery(id+"F1.opExtrude","CAP_EDGE",EDGE,{"disambiguationData":[OSD([sQuery(id+"F0.wireOp",EDGE,"E144")])],"isStart":false});
            var Q48;
            Q48=makeQuery(id+"F1.opExtrude","CAP_EDGE",EDGE,{"disambiguationData":[OSD([sQuery(id+"F0.wireOp",EDGE,"E147")])],"isStart":false});
            var Q49;
            Q49=makeQuery(id+"F1.opExtrude","CAP_EDGE",EDGE,{"disambiguationData":[OSD([sQuery(id+"F0.wireOp",EDGE,"E146")])],"isStart":false});
            var Q50;
            Q50=makeQuery(id+"F1.opExtrude","CAP_EDGE",EDGE,{"disambiguationData":[OSD([sQuery(id+"F0.wireOp",EDGE,"E145")])],"isStart":false});
            var Q51;
            Q51=makeQuery(id+"F1.opExtrude","CAP_EDGE",EDGE,{"disambiguationData":[OSD([sQuery(id+"F0.wireOp",EDGE,"E149")])],"isStart":false});
            var Q52;
            Q52=makeQuery(id+"F1.opExtrude","CAP_EDGE",EDGE,{"disambiguationData":[OSD([sQuery(id+"F0.wireOp",EDGE,"E150")])],"isStart":false});
            var Q53;
            Q53=makeQuery(id+"F1.opExtrude","CAP_EDGE",EDGE,{"disambiguationData":[OSD([sQuery(id+"F0.wireOp",EDGE,"E151")])],"isStart":false});
            var Q54;
            Q54=makeQuery(id+"F1.opExtrude","CAP_EDGE",EDGE,{"disambiguationData":[OSD([sQuery(id+"F0.wireOp",EDGE,"E148")])],"isStart":false});
            var Q55;
            Q55=makeQuery(id+"F1.opExtrude","CAP_EDGE",EDGE,{"disambiguationData":[OSD([sQuery(id+"F0.wireOp",EDGE,"E154")])],"isStart":false});
            var Q56;
            Q56=makeQuery(id+"F1.opExtrude","CAP_EDGE",EDGE,{"disambiguationData":[OSD([sQuery(id+"F0.wireOp",EDGE,"E90")])],"isStart":false});
            var Q57;
            Q57=makeQuery(id+"F1.opExtrude","CAP_EDGE",EDGE,{"disambiguationData":[OSD([sQuery(id+"F0.wireOp",EDGE,"E89")])],"isStart":false});
            var Q58;
            Q58=makeQuery(id+"F1.opExtrude","CAP_FACE",FACE,{"disambiguationData":[OSD([sQuery(id+"F0.wireOp",EDGE,"E88")])],"isStart":false});
            var Q59;
            Q59=makeQuery(id+"F1.opExtrude","CAP_EDGE",EDGE,{"disambiguationData":[OSD([sQuery(id+"F0.wireOp",EDGE,"E85")])],"isStart":false});
            var Q60;
            Q60=makeQuery(id+"F1.opExtrude","CAP_EDGE",EDGE,{"disambiguationData":[OSD([sQuery(id+"F0.wireOp",EDGE,"E84")])],"isStart":false});
            var Q61;
            Q61=makeQuery(id+"F1.opExtrude","CAP_EDGE",EDGE,{"disambiguationData":[OSD([sQuery(id+"F0.wireOp",EDGE,"E86")])],"isStart":false});
            var Q62;
            Q62=makeQuery(id+"F1.opExtrude","CAP_EDGE",EDGE,{"disambiguationData":[OSD([sQuery(id+"F0.wireOp",EDGE,"E87")])],"isStart":false});
            var Q63;
            Q63=makeQuery(id+"F1.opExtrude","CAP_EDGE",EDGE,{"disambiguationData":[OSD([sQuery(id+"F0.wireOp",EDGE,"E23")])],"isStart":false});
            var Q64;
            Q64=makeQuery(id+"F1.opExtrude","CAP_EDGE",EDGE,{"disambiguationData":[OSD([sQuery(id+"F0.wireOp",EDGE,"E22")])],"isStart":false});
            var Q65;
            Q65=makeQuery(id+"F1.opExtrude","CAP_EDGE",EDGE,{"disambiguationData":[OSD([sQuery(id+"F0.wireOp",EDGE,"E21")])],"isStart":false});
            var Q66;
            Q66=makeQuery(id+"F1.opExtrude","CAP_FACE",FACE,{"disambiguationData":[OSD([sQuery(id+"F0.wireOp",EDGE,"E20")])],"isStart":false});
            var Q67;
            Q67=makeQuery(id+"F1.opExtrude","CAP_EDGE",EDGE,{"disambiguationData":[OSD([sQuery(id+"F0.wireOp",EDGE,"E24")])],"isStart":false});
            var Q68;
            Q68=makeQuery(id+"F1.opExtrude","CAP_EDGE",EDGE,{"disambiguationData":[OSD([sQuery(id+"F0.wireOp",EDGE,"E25")])],"isStart":false});
            var Q69;
            Q69=makeQuery(id+"F1.opExtrude","CAP_EDGE",EDGE,{"disambiguationData":[OSD([sQuery(id+"F0.wireOp",EDGE,"E153")])],"isStart":false});
            var Q70;
            Q70=makeQuery(id+"F1.opExtrude","CAP_EDGE",EDGE,{"disambiguationData":[OSD([sQuery(id+"F0.wireOp",EDGE,"E152")])],"isStart":false});
            var Q71;
            Q71=makeQuery(id+"F1.opExtrude","CAP_EDGE",EDGE,{"disambiguationData":[OSD([sQuery(id+"F0.wireOp",EDGE,"E156")])],"isStart":false});
            var Q72;
            Q72=makeQuery(id+"F1.opExtrude","CAP_EDGE",EDGE,{"disambiguationData":[OSD([sQuery(id+"F0.wireOp",EDGE,"E157")])],"isStart":false});
            var Q73;
            Q73=makeQuery(id+"F1.opExtrude","CAP_EDGE",EDGE,{"disambiguationData":[OSD([sQuery(id+"F0.wireOp",EDGE,"E158")])],"isStart":false});
            var Q74;
            Q74=makeQuery(id+"F1.opExtrude","CAP_FACE",FACE,{"disambiguationData":[OSD([sQuery(id+"F0.wireOp",EDGE,"E91")])],"isStart":false});
            var Q75;
            Q75=makeQuery(id+"F1.opExtrude","CAP_EDGE",EDGE,{"disambiguationData":[OSD([sQuery(id+"F0.wireOp",EDGE,"E93")])],"isStart":false});
            var Q76;
            Q76=makeQuery(id+"F1.opExtrude","CAP_EDGE",EDGE,{"disambiguationData":[OSD([sQuery(id+"F0.wireOp",EDGE,"E92")])],"isStart":false});
            var Q77;
            Q77=makeQuery(id+"F1.opExtrude","CAP_EDGE",EDGE,{"disambiguationData":[OSD([sQuery(id+"F0.wireOp",EDGE,"E94")])],"isStart":false});
            var Q78;
            Q78=makeQuery(id+"F1.opExtrude","CAP_EDGE",EDGE,{"disambiguationData":[OSD([sQuery(id+"F0.wireOp",EDGE,"E28")])],"isStart":false});
            var Q79;
            Q79=makeQuery(id+"F1.opExtrude","CAP_FACE",FACE,{"disambiguationData":[OSD([sQuery(id+"F0.wireOp",EDGE,"E26")])],"isStart":false});
            var Q80;
            Q80=makeQuery(id+"F1.opExtrude","CAP_EDGE",EDGE,{"disambiguationData":[OSD([sQuery(id+"F0.wireOp",EDGE,"E27")])],"isStart":false});
            var Q81;
            Q81=makeQuery(id+"F1.opExtrude","CAP_EDGE",EDGE,{"disambiguationData":[OSD([sQuery(id+"F0.wireOp",EDGE,"E29")])],"isStart":false});
            var Q82;
            Q82=makeQuery(id+"F1.opExtrude","CAP_EDGE",EDGE,{"disambiguationData":[OSD([sQuery(id+"F0.wireOp",EDGE,"E30")])],"isStart":false});
            var Q83;
            Q83=makeQuery(id+"F1.opExtrude","CAP_EDGE",EDGE,{"disambiguationData":[OSD([sQuery(id+"F0.wireOp",EDGE,"E95")])],"isStart":false});
            var Q84;
            Q84=makeQuery(id+"F1.opExtrude","CAP_EDGE",EDGE,{"disambiguationData":[OSD([sQuery(id+"F0.wireOp",EDGE,"E96")])],"isStart":false});
            var Q85;
            Q85=makeQuery(id+"F1.opExtrude","CAP_EDGE",EDGE,{"disambiguationData":[OSD([sQuery(id+"F0.wireOp",EDGE,"E160")])],"isStart":false});
            var Q86;
            Q86=makeQuery(id+"F1.opExtrude","CAP_EDGE",EDGE,{"disambiguationData":[OSD([sQuery(id+"F0.wireOp",EDGE,"E159")])],"isStart":false});
            var Q87;
            Q87=makeQuery(id+"F1.opExtrude","CAP_FACE",FACE,{"disambiguationData":[OSD([sQuery(id+"F0.wireOp",EDGE,"E161")])],"isStart":false});
            var Q88;
            Q88=makeQuery(id+"F1.opExtrude","CAP_EDGE",EDGE,{"disambiguationData":[OSD([sQuery(id+"F0.wireOp",EDGE,"E162")])],"isStart":false});
            var Q89;
            Q89=makeQuery(id+"F1.opExtrude","CAP_EDGE",EDGE,{"disambiguationData":[OSD([sQuery(id+"F0.wireOp",EDGE,"E163")])],"isStart":false});
            var Q90;
            Q90=makeQuery(id+"F1.opExtrude","CAP_EDGE",EDGE,{"disambiguationData":[OSD([sQuery(id+"F0.wireOp",EDGE,"E164")])],"isStart":false});
            var Q91;
            Q91=makeQuery(id+"F1.opExtrude","CAP_EDGE",EDGE,{"disambiguationData":[OSD([sQuery(id+"F0.wireOp",EDGE,"E165")])],"isStart":false});
            var Q92;
            Q92=makeQuery(id+"F1.opExtrude","CAP_EDGE",EDGE,{"disambiguationData":[OSD([sQuery(id+"F0.wireOp",EDGE,"E99")])],"isStart":false});
            var Q93;
            Q93=makeQuery(id+"F1.opExtrude","CAP_EDGE",EDGE,{"disambiguationData":[OSD([sQuery(id+"F0.wireOp",EDGE,"E98")])],"isStart":false});
            var Q94;
            Q94=makeQuery(id+"F1.opExtrude","CAP_EDGE",EDGE,{"disambiguationData":[OSD([sQuery(id+"F0.wireOp",EDGE,"E97")])],"isStart":false});
            var Q95;
            Q95=makeQuery(id+"F1.opExtrude","CAP_EDGE",EDGE,{"disambiguationData":[OSD([sQuery(id+"F0.wireOp",EDGE,"E32")])],"isStart":false});
            var Q96;
            Q96=makeQuery(id+"F1.opExtrude","CAP_EDGE",EDGE,{"disambiguationData":[OSD([sQuery(id+"F0.wireOp",EDGE,"E31")])],"isStart":false});
            var Q97;
            Q97=makeQuery(id+"F1.opExtrude","CAP_EDGE",EDGE,{"disambiguationData":[OSD([sQuery(id+"F0.wireOp",EDGE,"E33")])],"isStart":false});
            var Q98;
            Q98=makeQuery(id+"F1.opExtrude","CAP_EDGE",EDGE,{"disambiguationData":[OSD([sQuery(id+"F0.wireOp",EDGE,"E37")])],"isStart":false});
            var Q99;
            Q99=makeQuery(id+"F1.opExtrude","CAP_EDGE",EDGE,{"disambiguationData":[OSD([sQuery(id+"F0.wireOp",EDGE,"E36")])],"isStart":false});
            var Q100;
            Q100=makeQuery(id+"F1.opExtrude","CAP_EDGE",EDGE,{"disambiguationData":[OSD([sQuery(id+"F0.wireOp",EDGE,"E35")])],"isStart":false});
            var Q101;
            Q101=makeQuery(id+"F1.opExtrude","CAP_EDGE",EDGE,{"disambiguationData":[OSD([sQuery(id+"F0.wireOp",EDGE,"E34")])],"isStart":false});
            var Q102;
            Q102=makeQuery(id+"F1.opExtrude","CAP_EDGE",EDGE,{"disambiguationData":[OSD([sQuery(id+"F0.wireOp",EDGE,"E38")])],"isStart":false});
            var Q103;
            Q103=makeQuery(id+"F1.opExtrude","CAP_EDGE",EDGE,{"disambiguationData":[OSD([sQuery(id+"F0.wireOp",EDGE,"E42")])],"isStart":false});
            var Q104;
            Q104=makeQuery(id+"F1.opExtrude","CAP_EDGE",EDGE,{"disambiguationData":[OSD([sQuery(id+"F0.wireOp",EDGE,"E41")])],"isStart":false});
            var Q105;
            Q105=makeQuery(id+"F1.opExtrude","CAP_EDGE",EDGE,{"disambiguationData":[OSD([sQuery(id+"F0.wireOp",EDGE,"E40")])],"isStart":false});
            var Q106;
            Q106=makeQuery(id+"F1.opExtrude","CAP_EDGE",EDGE,{"disambiguationData":[OSD([sQuery(id+"F0.wireOp",EDGE,"E39")])],"isStart":false});
            var Q107;
            Q107=makeQuery(id+"F1.opExtrude","CAP_EDGE",EDGE,{"disambiguationData":[OSD([sQuery(id+"F0.wireOp",EDGE,"E105")])],"isStart":false});
            var Q108;
            Q108=makeQuery(id+"F1.opExtrude","CAP_EDGE",EDGE,{"disambiguationData":[OSD([sQuery(id+"F0.wireOp",EDGE,"E106")])],"isStart":false});
            var Q109;
            Q109=makeQuery(id+"F1.opExtrude","CAP_EDGE",EDGE,{"disambiguationData":[OSD([sQuery(id+"F0.wireOp",EDGE,"E104")])],"isStart":false});
            var Q110;
            Q110=makeQuery(id+"F1.opExtrude","CAP_EDGE",EDGE,{"disambiguationData":[OSD([sQuery(id+"F0.wireOp",EDGE,"E103")])],"isStart":false});
            var Q111;
            Q111=makeQuery(id+"F1.opExtrude","CAP_EDGE",EDGE,{"disambiguationData":[OSD([sQuery(id+"F0.wireOp",EDGE,"E102")])],"isStart":false});
            var Q112;
            Q112=makeQuery(id+"F1.opExtrude","CAP_EDGE",EDGE,{"disambiguationData":[OSD([sQuery(id+"F0.wireOp",EDGE,"E101")])],"isStart":false});
            var Q113;
            Q113=makeQuery(id+"F1.opExtrude","CAP_FACE",FACE,{"disambiguationData":[OSD([sQuery(id+"F0.wireOp",EDGE,"E100")])],"isStart":false});
            var Q114;
            Q114=makeQuery(id+"F1.opExtrude","CAP_EDGE",EDGE,{"disambiguationData":[OSD([sQuery(id+"F0.wireOp",EDGE,"E107")])],"isStart":false});
            var Q115;
            Q115=makeQuery(id+"F1.opExtrude","CAP_EDGE",EDGE,{"disambiguationData":[OSD([sQuery(id+"F0.wireOp",EDGE,"E45")])],"isStart":false});
            var Q116;
            Q116=makeQuery(id+"F1.opExtrude","CAP_EDGE",EDGE,{"disambiguationData":[OSD([sQuery(id+"F0.wireOp",EDGE,"E43")])],"isStart":false});
            var Q117;
            Q117=makeQuery(id+"F1.opExtrude","CAP_EDGE",EDGE,{"disambiguationData":[OSD([sQuery(id+"F0.wireOp",EDGE,"E44")])],"isStart":false});
            var Q118;
            Q118=makeQuery(id+"F1.opExtrude","CAP_EDGE",EDGE,{"disambiguationData":[OSD([sQuery(id+"F0.wireOp",EDGE,"E46")])],"isStart":false});
            var Q119;
            Q119=makeQuery(id+"F1.opExtrude","CAP_EDGE",EDGE,{"disambiguationData":[OSD([sQuery(id+"F0.wireOp",EDGE,"E47")])],"isStart":false});
            var Q120;
            Q120=makeQuery(id+"F1.opExtrude","CAP_EDGE",EDGE,{"disambiguationData":[OSD([sQuery(id+"F0.wireOp",EDGE,"E48")])],"isStart":false});
            var Q121;
            Q121=makeQuery(id+"F1.opExtrude","CAP_EDGE",EDGE,{"disambiguationData":[OSD([sQuery(id+"F0.wireOp",EDGE,"E49")])],"isStart":false});
            var Q122;
            Q122=makeQuery(id+"F1.opExtrude","CAP_EDGE",EDGE,{"disambiguationData":[OSD([sQuery(id+"F0.wireOp",EDGE,"E108")])],"isStart":false});
            var Q123;
            Q123=makeQuery(id+"F1.opExtrude","CAP_EDGE",EDGE,{"disambiguationData":[OSD([sQuery(id+"F0.wireOp",EDGE,"E110")])],"isStart":false});
            var Q124;
            Q124=makeQuery(id+"F1.opExtrude","CAP_EDGE",EDGE,{"disambiguationData":[OSD([sQuery(id+"F0.wireOp",EDGE,"E109")])],"isStart":false});
            var Q125;
            Q125=makeQuery(id+"F1.opExtrude","CAP_EDGE",EDGE,{"disambiguationData":[OSD([sQuery(id+"F0.wireOp",EDGE,"E111")])],"isStart":false});
            var Q126;
            Q126=makeQuery(id+"F1.opExtrude","CAP_EDGE",EDGE,{"disambiguationData":[OSD([sQuery(id+"F0.wireOp",EDGE,"E112")])],"isStart":false});
            var Q127;
            Q127=makeQuery(id+"F1.opExtrude","CAP_EDGE",EDGE,{"disambiguationData":[OSD([sQuery(id+"F0.wireOp",EDGE,"E114")])],"isStart":false});
            var Q128;
            Q128=makeQuery(id+"F1.opExtrude","CAP_EDGE",EDGE,{"disambiguationData":[OSD([sQuery(id+"F0.wireOp",EDGE,"E116")])],"isStart":false});
            var Q129;
            Q129=makeQuery(id+"F1.opExtrude","CAP_EDGE",EDGE,{"disambiguationData":[OSD([sQuery(id+"F0.wireOp",EDGE,"E113")])],"isStart":false});
            var Q130;
            Q130=makeQuery(id+"F1.opExtrude","CAP_EDGE",EDGE,{"disambiguationData":[OSD([sQuery(id+"F0.wireOp",EDGE,"E115")])],"isStart":false});
            var Q131;
            Q131=makeQuery(id+"F1.opExtrude","CAP_EDGE",EDGE,{"disambiguationData":[OSD([sQuery(id+"F0.wireOp",EDGE,"E117")])],"isStart":false});
            var Q132;
            Q132=makeQuery(id+"F1.opExtrude","CAP_FACE",FACE,{"disambiguationData":[OSD([sQuery(id+"F0.wireOp",EDGE,"E118")])],"isStart":false});
            var Q133;
            Q133=makeQuery(id+"F1.opExtrude","CAP_EDGE",EDGE,{"disambiguationData":[OSD([sQuery(id+"F0.wireOp",EDGE,"E119")])],"isStart":false});
            var Q134;
            Q134=makeQuery(id+"F1.opExtrude","CAP_EDGE",EDGE,{"disambiguationData":[OSD([sQuery(id+"F0.wireOp",EDGE,"E56")])],"isStart":false});
            var Q135;
            Q135=makeQuery(id+"F1.opExtrude","CAP_EDGE",EDGE,{"disambiguationData":[OSD([sQuery(id+"F0.wireOp",EDGE,"E55")])],"isStart":false});
            var Q136;
            Q136=makeQuery(id+"F1.opExtrude","CAP_FACE",FACE,{"disambiguationData":[OSD([sQuery(id+"F0.wireOp",EDGE,"E53")])],"isStart":false});
            var Q137;
            Q137=makeQuery(id+"F1.opExtrude","CAP_EDGE",EDGE,{"disambiguationData":[OSD([sQuery(id+"F0.wireOp",EDGE,"E54")])],"isStart":false});
            var Q138;
            Q138=makeQuery(id+"F1.opExtrude","CAP_EDGE",EDGE,{"disambiguationData":[OSD([sQuery(id+"F0.wireOp",EDGE,"E53")])],"isStart":false});
            var Q139;
            Q139=makeQuery(id+"F1.opExtrude","CAP_EDGE",EDGE,{"disambiguationData":[OSD([sQuery(id+"F0.wireOp",EDGE,"E52")])],"isStart":false});
            var Q140;
            Q140=makeQuery(id+"F1.opExtrude","CAP_EDGE",EDGE,{"disambiguationData":[OSD([sQuery(id+"F0.wireOp",EDGE,"E50")])],"isStart":false});
            var Q141;
            Q141=makeQuery(id+"F1.opExtrude","CAP_EDGE",EDGE,{"disambiguationData":[OSD([sQuery(id+"F0.wireOp",EDGE,"E51")])],"isStart":false});
            var Q142;
            Q142=makeQuery(id+"F1.opExtrude","CAP_EDGE",EDGE,{"disambiguationData":[OSD([sQuery(id+"F0.wireOp",EDGE,"E120")])],"isStart":false});
            var Q143;
            Q143=makeQuery(id+"F1.opExtrude","CAP_EDGE",EDGE,{"disambiguationData":[OSD([sQuery(id+"F0.wireOp",EDGE,"E121")])],"isStart":false});
            var Q144;
            Q144=makeQuery(id+"F1.opExtrude","CAP_EDGE",EDGE,{"disambiguationData":[OSD([sQuery(id+"F0.wireOp",EDGE,"E122")])],"isStart":false});
            var Q145;
            Q145=makeQuery(id+"F1.opExtrude","CAP_EDGE",EDGE,{"disambiguationData":[OSD([sQuery(id+"F0.wireOp",EDGE,"E123")])],"isStart":false});
            var Q146;
            Q146=makeQuery(id+"F1.opExtrude","CAP_EDGE",EDGE,{"disambiguationData":[OSD([sQuery(id+"F0.wireOp",EDGE,"E59")])],"isStart":false});
            var Q147;
            Q147=makeQuery(id+"F1.opExtrude","CAP_EDGE",EDGE,{"disambiguationData":[OSD([sQuery(id+"F0.wireOp",EDGE,"E58")])],"isStart":false});
            var Q148;
            Q148=makeQuery(id+"F1.opExtrude","CAP_EDGE",EDGE,{"disambiguationData":[OSD([sQuery(id+"F0.wireOp",EDGE,"E57")])],"isStart":false});
            var Q149;
            Q149=makeQuery(id+"F1.opExtrude","CAP_EDGE",EDGE,{"disambiguationData":[OSD([sQuery(id+"F0.wireOp",EDGE,"E60")])],"isStart":false});
            var Q150;
            Q150=makeQuery(id+"F1.opExtrude","CAP_EDGE",EDGE,{"disambiguationData":[OSD([sQuery(id+"F0.wireOp",EDGE,"E129")])],"isStart":false});
            var Q151;
            Q151=makeQuery(id+"F1.opExtrude","CAP_EDGE",EDGE,{"disambiguationData":[OSD([sQuery(id+"F0.wireOp",EDGE,"E128")])],"isStart":false});
            var Q152;
            Q152=makeQuery(id+"F1.opExtrude","CAP_EDGE",EDGE,{"disambiguationData":[OSD([sQuery(id+"F0.wireOp",EDGE,"E127")])],"isStart":false});
            var Q153;
            Q153=makeQuery(id+"F1.opExtrude","CAP_EDGE",EDGE,{"disambiguationData":[OSD([sQuery(id+"F0.wireOp",EDGE,"E130")])],"isStart":false});
            var Q154;
            Q154=makeQuery(id+"F1.opExtrude","CAP_FACE",FACE,{"disambiguationData":[OSD([sQuery(id+"F0.wireOp",EDGE,"E126")])],"isStart":false});
            var Q155;
            Q155=makeQuery(id+"F1.opExtrude","CAP_FACE",FACE,{"disambiguationData":[OSD([sQuery(id+"F0.wireOp",EDGE,"E67")])],"isStart":false});
            var Q156;
            Q156=makeQuery(id+"F1.opExtrude","CAP_EDGE",EDGE,{"disambiguationData":[OSD([sQuery(id+"F0.wireOp",EDGE,"E66")])],"isStart":false});
            var Q157;
            Q157=makeQuery(id+"F1.opExtrude","CAP_EDGE",EDGE,{"disambiguationData":[OSD([sQuery(id+"F0.wireOp",EDGE,"E64")])],"isStart":false});
            var Q158;
            Q158=makeQuery(id+"F1.opExtrude","CAP_FACE",FACE,{"disambiguationData":[OSD([sQuery(id+"F0.wireOp",EDGE,"E65")])],"isStart":false});
            var Q159;
            Q159=makeQuery(id+"F1.opExtrude","CAP_FACE",FACE,{"disambiguationData":[OSD([sQuery(id+"F0.wireOp",EDGE,"E63")])],"isStart":false});
            var Q160;
            Q160=makeQuery(id+"F1.opExtrude","CAP_FACE",FACE,{"disambiguationData":[OSD([sQuery(id+"F0.wireOp",EDGE,"E62")])],"isStart":false});
            var Q161;
            Q161=makeQuery(id+"F1.opExtrude","CAP_FACE",FACE,{"disambiguationData":[OSD([sQuery(id+"F0.wireOp",EDGE,"E61")])],"isStart":false});
            var Q162;
            Q162=makeQuery(id+"F1.opExtrude","CAP_FACE",FACE,{"disambiguationData":[OSD([sQuery(id+"F0.wireOp",EDGE,"E124")])],"isStart":false});
            var Q163;
            Q163=makeQuery(id+"F1.opExtrude","CAP_EDGE",EDGE,{"disambiguationData":[OSD([sQuery(id+"F0.wireOp",EDGE,"E125")])],"isStart":false});
            var Q164;
            Q164=makeQuery(id+"F1.opExtrude","CAP_EDGE",EDGE,{"disambiguationData":[OSD([sQuery(id+"F0.wireOp",EDGE,"E155")])],"isStart":false});
            var Q165;
            Q165=makeQuery(id+"F1.opExtrude","CAP_EDGE",EDGE,{"disambiguationData":[OSD([sQuery(id+"F0.wireOp",EDGE,"E0")])],"isStart":false});
            fillet(context, id + "F2", {"entities" : qUnion([Q0, Q1, Q2, Q3, Q4, Q5, Q6, Q7, Q8, Q9, Q10, Q11, Q12, Q13, Q14, Q15, Q16, Q17, Q18, Q19, Q20, Q21, Q22, Q23, Q24, Q25, Q26, Q27, Q28, Q29, Q30, Q31, Q32, Q33, Q34, Q35, Q36, Q37, Q38, Q39, Q40, Q41, Q42, Q43, Q44, Q45, Q46, Q47, Q48, Q49, Q50, Q51, Q52, Q53, Q54, Q55, Q56, Q57, Q58, Q59, Q60, Q61, Q62, Q63, Q64, Q65, Q66, Q67, Q68, Q69, Q70, Q71, Q72, Q73, Q74, Q75, Q76, Q77, Q78, Q79, Q80, Q81, Q82, Q83, Q84, Q85, Q86, Q87, Q88, Q89, Q90, Q91, Q92, Q93, Q94, Q95, Q96, Q97, Q98, Q99, Q100, Q101, Q102, Q103, Q104, Q105, Q106, Q107, Q108, Q109, Q110, Q111, Q112, Q113, Q114, Q115, Q116, Q117, Q118, Q119, Q120, Q121, Q122, Q123, Q124, Q125, Q126, Q127, Q128, Q129, Q130, Q131, Q132, Q133, Q134, Q135, Q136, Q137, Q138, Q139, Q140, Q141, Q142, Q143, Q144, Q145, Q146, Q147, Q148, Q149, Q150, Q151, Q152, Q153, Q154, Q155, Q156, Q157, Q158, Q159, Q160, Q161, Q162, Q163, Q164, Q165]), "radius" : 0.6 * mm, "rho" : .3, "crossSection" : FilletCrossSection.CONIC, "allowEdgeOverflow" : false});
        }
        {
            var Q0;
            Q0=makeQuery(id+"F1.opExtrude","SWEPT_BODY",BODY,{"disambiguationData":[OSD([sQuery(id+"F0.wireOp",EDGE,"E0")])]});
            var Q1;
            Q1=makeQuery(id+"F1.opExtrude","SWEPT_BODY",BODY,{"disambiguationData":[OSD([sQuery(id+"F0.wireOp",EDGE,"E1")])]});
            var Q2;
            Q2=makeQuery(id+"F1.opExtrude","SWEPT_BODY",BODY,{"disambiguationData":[OSD([sQuery(id+"F0.wireOp",EDGE,"E2")])]});
            var Q3;
            Q3=makeQuery(id+"F1.opExtrude","SWEPT_BODY",BODY,{"disambiguationData":[OSD([sQuery(id+"F0.wireOp",EDGE,"E3")])]});
            var Q4;
            Q4=makeQuery(id+"F1.opExtrude","SWEPT_BODY",BODY,{"disambiguationData":[OSD([sQuery(id+"F0.wireOp",EDGE,"E4")])]});
            var Q5;
            Q5=makeQuery(id+"F1.opExtrude","SWEPT_BODY",BODY,{"disambiguationData":[OSD([sQuery(id+"F0.wireOp",EDGE,"E5")])]});
            var Q6;
            Q6=makeQuery(id+"F1.opExtrude","SWEPT_BODY",BODY,{"disambiguationData":[OSD([sQuery(id+"F0.wireOp",EDGE,"E6")])]});
            var Q7;
            Q7=makeQuery(id+"F1.opExtrude","SWEPT_BODY",BODY,{"disambiguationData":[OSD([sQuery(id+"F0.wireOp",EDGE,"E7")])]});
            var Q8;
            Q8=makeQuery(id+"F1.opExtrude","SWEPT_BODY",BODY,{"disambiguationData":[OSD([sQuery(id+"F0.wireOp",EDGE,"E8")])]});
            var Q9;
            Q9=makeQuery(id+"F1.opExtrude","SWEPT_BODY",BODY,{"disambiguationData":[OSD([sQuery(id+"F0.wireOp",EDGE,"E9")])]});
            var Q10;
            Q10=makeQuery(id+"F1.opExtrude","SWEPT_BODY",BODY,{"disambiguationData":[OSD([sQuery(id+"F0.wireOp",EDGE,"E10")])]});
            var Q11;
            Q11=makeQuery(id+"F1.opExtrude","SWEPT_BODY",BODY,{"disambiguationData":[OSD([sQuery(id+"F0.wireOp",EDGE,"E11")])]});
            var Q12;
            Q12=makeQuery(id+"F1.opExtrude","SWEPT_BODY",BODY,{"disambiguationData":[OSD([sQuery(id+"F0.wireOp",EDGE,"E12")])]});
            var Q13;
            Q13=makeQuery(id+"F1.opExtrude","SWEPT_BODY",BODY,{"disambiguationData":[OSD([sQuery(id+"F0.wireOp",EDGE,"E13")])]});
            var Q14;
            Q14=makeQuery(id+"F1.opExtrude","SWEPT_BODY",BODY,{"disambiguationData":[OSD([sQuery(id+"F0.wireOp",EDGE,"E14")])]});
            var Q15;
            Q15=makeQuery(id+"F1.opExtrude","SWEPT_BODY",BODY,{"disambiguationData":[OSD([sQuery(id+"F0.wireOp",EDGE,"E15")])]});
            var Q16;
            Q16=makeQuery(id+"F1.opExtrude","SWEPT_BODY",BODY,{"disambiguationData":[OSD([sQuery(id+"F0.wireOp",EDGE,"E16")])]});
            var Q17;
            Q17=makeQuery(id+"F1.opExtrude","SWEPT_BODY",BODY,{"disambiguationData":[OSD([sQuery(id+"F0.wireOp",EDGE,"E17")])]});
            var Q18;
            Q18=makeQuery(id+"F1.opExtrude","SWEPT_BODY",BODY,{"disambiguationData":[OSD([sQuery(id+"F0.wireOp",EDGE,"E18")])]});
            var Q19;
            Q19=makeQuery(id+"F1.opExtrude","SWEPT_BODY",BODY,{"disambiguationData":[OSD([sQuery(id+"F0.wireOp",EDGE,"E20")])]});
            var Q20;
            Q20=makeQuery(id+"F1.opExtrude","SWEPT_BODY",BODY,{"disambiguationData":[OSD([sQuery(id+"F0.wireOp",EDGE,"E21")])]});
            var Q21;
            Q21=makeQuery(id+"F1.opExtrude","SWEPT_BODY",BODY,{"disambiguationData":[OSD([sQuery(id+"F0.wireOp",EDGE,"E22")])]});
            var Q22;
            Q22=makeQuery(id+"F1.opExtrude","SWEPT_BODY",BODY,{"disambiguationData":[OSD([sQuery(id+"F0.wireOp",EDGE,"E23")])]});
            var Q23;
            Q23=makeQuery(id+"F1.opExtrude","SWEPT_BODY",BODY,{"disambiguationData":[OSD([sQuery(id+"F0.wireOp",EDGE,"E24")])]});
            var Q24;
            Q24=makeQuery(id+"F1.opExtrude","SWEPT_BODY",BODY,{"disambiguationData":[OSD([sQuery(id+"F0.wireOp",EDGE,"E25")])]});
            var Q25;
            Q25=makeQuery(id+"F1.opExtrude","SWEPT_BODY",BODY,{"disambiguationData":[OSD([sQuery(id+"F0.wireOp",EDGE,"E26")])]});
            var Q26;
            Q26=makeQuery(id+"F1.opExtrude","SWEPT_BODY",BODY,{"disambiguationData":[OSD([sQuery(id+"F0.wireOp",EDGE,"E27")])]});
            var Q27;
            Q27=makeQuery(id+"F1.opExtrude","SWEPT_BODY",BODY,{"disambiguationData":[OSD([sQuery(id+"F0.wireOp",EDGE,"E28")])]});
            var Q28;
            Q28=makeQuery(id+"F1.opExtrude","SWEPT_BODY",BODY,{"disambiguationData":[OSD([sQuery(id+"F0.wireOp",EDGE,"E29")])]});
            var Q29;
            Q29=makeQuery(id+"F1.opExtrude","SWEPT_BODY",BODY,{"disambiguationData":[OSD([sQuery(id+"F0.wireOp",EDGE,"E30")])]});
            var Q30;
            Q30=makeQuery(id+"F1.opExtrude","SWEPT_BODY",BODY,{"disambiguationData":[OSD([sQuery(id+"F0.wireOp",EDGE,"E31")])]});
            var Q31;
            Q31=makeQuery(id+"F1.opExtrude","SWEPT_BODY",BODY,{"disambiguationData":[OSD([sQuery(id+"F0.wireOp",EDGE,"E32")])]});
            var Q32;
            Q32=makeQuery(id+"F1.opExtrude","SWEPT_BODY",BODY,{"disambiguationData":[OSD([sQuery(id+"F0.wireOp",EDGE,"E33")])]});
            var Q33;
            Q33=makeQuery(id+"F1.opExtrude","SWEPT_BODY",BODY,{"disambiguationData":[OSD([sQuery(id+"F0.wireOp",EDGE,"E34")])]});
            var Q34;
            Q34=makeQuery(id+"F1.opExtrude","SWEPT_BODY",BODY,{"disambiguationData":[OSD([sQuery(id+"F0.wireOp",EDGE,"E35")])]});
            var Q35;
            Q35=makeQuery(id+"F1.opExtrude","SWEPT_BODY",BODY,{"disambiguationData":[OSD([sQuery(id+"F0.wireOp",EDGE,"E36")])]});
            var Q36;
            Q36=makeQuery(id+"F1.opExtrude","SWEPT_BODY",BODY,{"disambiguationData":[OSD([sQuery(id+"F0.wireOp",EDGE,"E37")])]});
            var Q37;
            Q37=makeQuery(id+"F1.opExtrude","SWEPT_BODY",BODY,{"disambiguationData":[OSD([sQuery(id+"F0.wireOp",EDGE,"E38")])]});
            var Q38;
            Q38=makeQuery(id+"F1.opExtrude","SWEPT_BODY",BODY,{"disambiguationData":[OSD([sQuery(id+"F0.wireOp",EDGE,"E39")])]});
            var Q39;
            Q39=makeQuery(id+"F1.opExtrude","SWEPT_BODY",BODY,{"disambiguationData":[OSD([sQuery(id+"F0.wireOp",EDGE,"E40")])]});
            var Q40;
            Q40=makeQuery(id+"F1.opExtrude","SWEPT_BODY",BODY,{"disambiguationData":[OSD([sQuery(id+"F0.wireOp",EDGE,"E41")])]});
            var Q41;
            Q41=makeQuery(id+"F1.opExtrude","SWEPT_BODY",BODY,{"disambiguationData":[OSD([sQuery(id+"F0.wireOp",EDGE,"E42")])]});
            var Q42;
            Q42=makeQuery(id+"F1.opExtrude","SWEPT_BODY",BODY,{"disambiguationData":[OSD([sQuery(id+"F0.wireOp",EDGE,"E43")])]});
            var Q43;
            Q43=makeQuery(id+"F1.opExtrude","SWEPT_BODY",BODY,{"disambiguationData":[OSD([sQuery(id+"F0.wireOp",EDGE,"E44")])]});
            var Q44;
            Q44=makeQuery(id+"F1.opExtrude","SWEPT_BODY",BODY,{"disambiguationData":[OSD([sQuery(id+"F0.wireOp",EDGE,"E45")])]});
            var Q45;
            Q45=makeQuery(id+"F1.opExtrude","SWEPT_BODY",BODY,{"disambiguationData":[OSD([sQuery(id+"F0.wireOp",EDGE,"E46")])]});
            var Q46;
            Q46=makeQuery(id+"F1.opExtrude","SWEPT_BODY",BODY,{"disambiguationData":[OSD([sQuery(id+"F0.wireOp",EDGE,"E47")])]});
            var Q47;
            Q47=makeQuery(id+"F1.opExtrude","SWEPT_BODY",BODY,{"disambiguationData":[OSD([sQuery(id+"F0.wireOp",EDGE,"E48")])]});
            var Q48;
            Q48=makeQuery(id+"F1.opExtrude","SWEPT_BODY",BODY,{"disambiguationData":[OSD([sQuery(id+"F0.wireOp",EDGE,"E49")])]});
            var Q49;
            Q49=makeQuery(id+"F1.opExtrude","SWEPT_BODY",BODY,{"disambiguationData":[OSD([sQuery(id+"F0.wireOp",EDGE,"E50")])]});
            var Q50;
            Q50=makeQuery(id+"F1.opExtrude","SWEPT_BODY",BODY,{"disambiguationData":[OSD([sQuery(id+"F0.wireOp",EDGE,"E51")])]});
            var Q51;
            Q51=makeQuery(id+"F1.opExtrude","SWEPT_BODY",BODY,{"disambiguationData":[OSD([sQuery(id+"F0.wireOp",EDGE,"E52")])]});
            var Q52;
            Q52=makeQuery(id+"F1.opExtrude","SWEPT_BODY",BODY,{"disambiguationData":[OSD([sQuery(id+"F0.wireOp",EDGE,"E53")])]});
            var Q53;
            Q53=makeQuery(id+"F1.opExtrude","SWEPT_BODY",BODY,{"disambiguationData":[OSD([sQuery(id+"F0.wireOp",EDGE,"E54")])]});
            var Q54;
            Q54=makeQuery(id+"F1.opExtrude","SWEPT_BODY",BODY,{"disambiguationData":[OSD([sQuery(id+"F0.wireOp",EDGE,"E55")])]});
            var Q55;
            Q55=makeQuery(id+"F1.opExtrude","SWEPT_BODY",BODY,{"disambiguationData":[OSD([sQuery(id+"F0.wireOp",EDGE,"E56")])]});
            var Q56;
            Q56=sQuery(id+"F0.wireOp",VERTEX,"E0.center");
            transform(context, id + "F3", {"entities" : qUnion([Q0, Q1, Q2, Q3, Q4, Q5, Q6, Q7, Q8, Q9, Q10, Q11, Q12, Q13, Q14, Q15, Q16, Q17, Q18, Q19, Q20, Q21, Q22, Q23, Q24, Q25, Q26, Q27, Q28, Q29, Q30, Q31, Q32, Q33, Q34, Q35, Q36, Q37, Q38, Q39, Q40, Q41, Q42, Q43, Q44, Q45, Q46, Q47, Q48, Q49, Q50, Q51, Q52, Q53, Q54, Q55]), "transformType" : TransformType.SCALE_UNIFORMLY, "scale" : 1.15, "scalePoint" : qUnion([Q56]), "makeCopy" : false});
        }
        {
            var Q0;
            Q0=makeQuery(id+"F1.opExtrude","SWEPT_BODY",BODY,{"disambiguationData":[OSD([sQuery(id+"F0.wireOp",EDGE,"E82")])]});
            var Q1;
            Q1=makeQuery(id+"F1.opExtrude","SWEPT_BODY",BODY,{"disambiguationData":[OSD([sQuery(id+"F0.wireOp",EDGE,"E83")])]});
            var Q2;
            Q2=makeQuery(id+"F1.opExtrude","SWEPT_BODY",BODY,{"disambiguationData":[OSD([sQuery(id+"F0.wireOp",EDGE,"E57")])]});
            var Q3;
            Q3=makeQuery(id+"F1.opExtrude","SWEPT_BODY",BODY,{"disambiguationData":[OSD([sQuery(id+"F0.wireOp",EDGE,"E58")])]});
            var Q4;
            Q4=makeQuery(id+"F1.opExtrude","SWEPT_BODY",BODY,{"disambiguationData":[OSD([sQuery(id+"F0.wireOp",EDGE,"E60")])]});
            var Q5;
            Q5=makeQuery(id+"F1.opExtrude","SWEPT_BODY",BODY,{"disambiguationData":[OSD([sQuery(id+"F0.wireOp",EDGE,"E61")])]});
            var Q6;
            Q6=makeQuery(id+"F1.opExtrude","SWEPT_BODY",BODY,{"disambiguationData":[OSD([sQuery(id+"F0.wireOp",EDGE,"E62")])]});
            var Q7;
            Q7=makeQuery(id+"F1.opExtrude","SWEPT_BODY",BODY,{"disambiguationData":[OSD([sQuery(id+"F0.wireOp",EDGE,"E63")])]});
            var Q8;
            Q8=makeQuery(id+"F1.opExtrude","SWEPT_BODY",BODY,{"disambiguationData":[OSD([sQuery(id+"F0.wireOp",EDGE,"E64")])]});
            var Q9;
            Q9=makeQuery(id+"F1.opExtrude","SWEPT_BODY",BODY,{"disambiguationData":[OSD([sQuery(id+"F0.wireOp",EDGE,"E65")])]});
            var Q10;
            Q10=makeQuery(id+"F1.opExtrude","SWEPT_BODY",BODY,{"disambiguationData":[OSD([sQuery(id+"F0.wireOp",EDGE,"E66")])]});
            var Q11;
            Q11=makeQuery(id+"F1.opExtrude","SWEPT_BODY",BODY,{"disambiguationData":[OSD([sQuery(id+"F0.wireOp",EDGE,"E67")])]});
            var Q12;
            Q12=makeQuery(id+"F1.opExtrude","SWEPT_BODY",BODY,{"disambiguationData":[OSD([sQuery(id+"F0.wireOp",EDGE,"E68")])]});
            var Q13;
            Q13=makeQuery(id+"F1.opExtrude","SWEPT_BODY",BODY,{"disambiguationData":[OSD([sQuery(id+"F0.wireOp",EDGE,"E69")])]});
            var Q14;
            Q14=makeQuery(id+"F1.opExtrude","SWEPT_BODY",BODY,{"disambiguationData":[OSD([sQuery(id+"F0.wireOp",EDGE,"E70")])]});
            var Q15;
            Q15=makeQuery(id+"F1.opExtrude","SWEPT_BODY",BODY,{"disambiguationData":[OSD([sQuery(id+"F0.wireOp",EDGE,"E71")])]});
            var Q16;
            Q16=makeQuery(id+"F1.opExtrude","SWEPT_BODY",BODY,{"disambiguationData":[OSD([sQuery(id+"F0.wireOp",EDGE,"E72")])]});
            var Q17;
            Q17=makeQuery(id+"F1.opExtrude","SWEPT_BODY",BODY,{"disambiguationData":[OSD([sQuery(id+"F0.wireOp",EDGE,"E73")])]});
            var Q18;
            Q18=makeQuery(id+"F1.opExtrude","SWEPT_BODY",BODY,{"disambiguationData":[OSD([sQuery(id+"F0.wireOp",EDGE,"E74")])]});
            var Q19;
            Q19=makeQuery(id+"F1.opExtrude","SWEPT_BODY",BODY,{"disambiguationData":[OSD([sQuery(id+"F0.wireOp",EDGE,"E75")])]});
            var Q20;
            Q20=makeQuery(id+"F1.opExtrude","SWEPT_BODY",BODY,{"disambiguationData":[OSD([sQuery(id+"F0.wireOp",EDGE,"E76")])]});
            var Q21;
            Q21=makeQuery(id+"F1.opExtrude","SWEPT_BODY",BODY,{"disambiguationData":[OSD([sQuery(id+"F0.wireOp",EDGE,"E77")])]});
            var Q22;
            Q22=makeQuery(id+"F1.opExtrude","SWEPT_BODY",BODY,{"disambiguationData":[OSD([sQuery(id+"F0.wireOp",EDGE,"E78")])]});
            var Q23;
            Q23=makeQuery(id+"F1.opExtrude","SWEPT_BODY",BODY,{"disambiguationData":[OSD([sQuery(id+"F0.wireOp",EDGE,"E79")])]});
            var Q24;
            Q24=makeQuery(id+"F1.opExtrude","SWEPT_BODY",BODY,{"disambiguationData":[OSD([sQuery(id+"F0.wireOp",EDGE,"E80")])]});
            var Q25;
            Q25=makeQuery(id+"F1.opExtrude","SWEPT_BODY",BODY,{"disambiguationData":[OSD([sQuery(id+"F0.wireOp",EDGE,"E81")])]});
            var Q26;
            Q26=makeQuery(id+"F1.opExtrude","SWEPT_BODY",BODY,{"disambiguationData":[OSD([sQuery(id+"F0.wireOp",EDGE,"E84")])]});
            var Q27;
            Q27=makeQuery(id+"F1.opExtrude","SWEPT_BODY",BODY,{"disambiguationData":[OSD([sQuery(id+"F0.wireOp",EDGE,"E85")])]});
            var Q28;
            Q28=makeQuery(id+"F1.opExtrude","SWEPT_BODY",BODY,{"disambiguationData":[OSD([sQuery(id+"F0.wireOp",EDGE,"E86")])]});
            var Q29;
            Q29=makeQuery(id+"F1.opExtrude","SWEPT_BODY",BODY,{"disambiguationData":[OSD([sQuery(id+"F0.wireOp",EDGE,"E87")])]});
            var Q30;
            Q30=makeQuery(id+"F1.opExtrude","SWEPT_BODY",BODY,{"disambiguationData":[OSD([sQuery(id+"F0.wireOp",EDGE,"E88")])]});
            var Q31;
            Q31=makeQuery(id+"F1.opExtrude","SWEPT_BODY",BODY,{"disambiguationData":[OSD([sQuery(id+"F0.wireOp",EDGE,"E89")])]});
            var Q32;
            Q32=makeQuery(id+"F1.opExtrude","SWEPT_BODY",BODY,{"disambiguationData":[OSD([sQuery(id+"F0.wireOp",EDGE,"E90")])]});
            var Q33;
            Q33=makeQuery(id+"F1.opExtrude","SWEPT_BODY",BODY,{"disambiguationData":[OSD([sQuery(id+"F0.wireOp",EDGE,"E91")])]});
            var Q34;
            Q34=makeQuery(id+"F1.opExtrude","SWEPT_BODY",BODY,{"disambiguationData":[OSD([sQuery(id+"F0.wireOp",EDGE,"E92")])]});
            var Q35;
            Q35=makeQuery(id+"F1.opExtrude","SWEPT_BODY",BODY,{"disambiguationData":[OSD([sQuery(id+"F0.wireOp",EDGE,"E93")])]});
            var Q36;
            Q36=makeQuery(id+"F1.opExtrude","SWEPT_BODY",BODY,{"disambiguationData":[OSD([sQuery(id+"F0.wireOp",EDGE,"E94")])]});
            var Q37;
            Q37=makeQuery(id+"F1.opExtrude","SWEPT_BODY",BODY,{"disambiguationData":[OSD([sQuery(id+"F0.wireOp",EDGE,"E95")])]});
            var Q38;
            Q38=makeQuery(id+"F1.opExtrude","SWEPT_BODY",BODY,{"disambiguationData":[OSD([sQuery(id+"F0.wireOp",EDGE,"E96")])]});
            var Q39;
            Q39=makeQuery(id+"F1.opExtrude","SWEPT_BODY",BODY,{"disambiguationData":[OSD([sQuery(id+"F0.wireOp",EDGE,"E97")])]});
            var Q40;
            Q40=makeQuery(id+"F1.opExtrude","SWEPT_BODY",BODY,{"disambiguationData":[OSD([sQuery(id+"F0.wireOp",EDGE,"E98")])]});
            var Q41;
            Q41=makeQuery(id+"F1.opExtrude","SWEPT_BODY",BODY,{"disambiguationData":[OSD([sQuery(id+"F0.wireOp",EDGE,"E99")])]});
            var Q42;
            Q42=makeQuery(id+"F1.opExtrude","SWEPT_BODY",BODY,{"disambiguationData":[OSD([sQuery(id+"F0.wireOp",EDGE,"E100")])]});
            var Q43;
            Q43=makeQuery(id+"F1.opExtrude","SWEPT_BODY",BODY,{"disambiguationData":[OSD([sQuery(id+"F0.wireOp",EDGE,"E101")])]});
            var Q44;
            Q44=makeQuery(id+"F1.opExtrude","SWEPT_BODY",BODY,{"disambiguationData":[OSD([sQuery(id+"F0.wireOp",EDGE,"E102")])]});
            var Q45;
            Q45=makeQuery(id+"F1.opExtrude","SWEPT_BODY",BODY,{"disambiguationData":[OSD([sQuery(id+"F0.wireOp",EDGE,"E103")])]});
            var Q46;
            Q46=makeQuery(id+"F1.opExtrude","SWEPT_BODY",BODY,{"disambiguationData":[OSD([sQuery(id+"F0.wireOp",EDGE,"E104")])]});
            var Q47;
            Q47=makeQuery(id+"F1.opExtrude","SWEPT_BODY",BODY,{"disambiguationData":[OSD([sQuery(id+"F0.wireOp",EDGE,"E105")])]});
            var Q48;
            Q48=makeQuery(id+"F1.opExtrude","SWEPT_BODY",BODY,{"disambiguationData":[OSD([sQuery(id+"F0.wireOp",EDGE,"E106")])]});
            var Q49;
            Q49=makeQuery(id+"F1.opExtrude","SWEPT_BODY",BODY,{"disambiguationData":[OSD([sQuery(id+"F0.wireOp",EDGE,"E107")])]});
            var Q50;
            Q50=sQuery(id+"F0.wireOp",VERTEX,"E59.center");
            transform(context, id + "F4", {"entities" : qUnion([Q0, Q1, Q2, Q3, Q4, Q5, Q6, Q7, Q8, Q9, Q10, Q11, Q12, Q13, Q14, Q15, Q16, Q17, Q18, Q19, Q20, Q21, Q22, Q23, Q24, Q25, Q26, Q27, Q28, Q29, Q30, Q31, Q32, Q33, Q34, Q35, Q36, Q37, Q38, Q39, Q40, Q41, Q42, Q43, Q44, Q45, Q46, Q47, Q48, Q49]), "transformType" : TransformType.SCALE_UNIFORMLY, "scale" : 1.15, "scalePoint" : qUnion([Q50]), "makeCopy" : false});
        }
        {
            var Q0;
            Q0=makeQuery(id+"F1.opExtrude","SWEPT_BODY",BODY,{"disambiguationData":[OSD([sQuery(id+"F0.wireOp",EDGE,"E122")])]});
            var Q1;
            Q1=makeQuery(id+"F1.opExtrude","SWEPT_BODY",BODY,{"disambiguationData":[OSD([sQuery(id+"F0.wireOp",EDGE,"E148")])]});
            var Q2;
            Q2=makeQuery(id+"F1.opExtrude","SWEPT_BODY",BODY,{"disambiguationData":[OSD([sQuery(id+"F0.wireOp",EDGE,"E108")])]});
            var Q3;
            Q3=makeQuery(id+"F1.opExtrude","SWEPT_BODY",BODY,{"disambiguationData":[OSD([sQuery(id+"F0.wireOp",EDGE,"E109")])]});
            var Q4;
            Q4=makeQuery(id+"F1.opExtrude","SWEPT_BODY",BODY,{"disambiguationData":[OSD([sQuery(id+"F0.wireOp",EDGE,"E110")])]});
            var Q5;
            Q5=makeQuery(id+"F1.opExtrude","SWEPT_BODY",BODY,{"disambiguationData":[OSD([sQuery(id+"F0.wireOp",EDGE,"E111")])]});
            var Q6;
            Q6=makeQuery(id+"F1.opExtrude","SWEPT_BODY",BODY,{"disambiguationData":[OSD([sQuery(id+"F0.wireOp",EDGE,"E112")])]});
            var Q7;
            Q7=makeQuery(id+"F1.opExtrude","SWEPT_BODY",BODY,{"disambiguationData":[OSD([sQuery(id+"F0.wireOp",EDGE,"E113")])]});
            var Q8;
            Q8=makeQuery(id+"F1.opExtrude","SWEPT_BODY",BODY,{"disambiguationData":[OSD([sQuery(id+"F0.wireOp",EDGE,"E114")])]});
            var Q9;
            Q9=makeQuery(id+"F1.opExtrude","SWEPT_BODY",BODY,{"disambiguationData":[OSD([sQuery(id+"F0.wireOp",EDGE,"E115")])]});
            var Q10;
            Q10=makeQuery(id+"F1.opExtrude","SWEPT_BODY",BODY,{"disambiguationData":[OSD([sQuery(id+"F0.wireOp",EDGE,"E116")])]});
            var Q11;
            Q11=makeQuery(id+"F1.opExtrude","SWEPT_BODY",BODY,{"disambiguationData":[OSD([sQuery(id+"F0.wireOp",EDGE,"E117")])]});
            var Q12;
            Q12=makeQuery(id+"F1.opExtrude","SWEPT_BODY",BODY,{"disambiguationData":[OSD([sQuery(id+"F0.wireOp",EDGE,"E118")])]});
            var Q13;
            Q13=makeQuery(id+"F1.opExtrude","SWEPT_BODY",BODY,{"disambiguationData":[OSD([sQuery(id+"F0.wireOp",EDGE,"E119")])]});
            var Q14;
            Q14=makeQuery(id+"F1.opExtrude","SWEPT_BODY",BODY,{"disambiguationData":[OSD([sQuery(id+"F0.wireOp",EDGE,"E120")])]});
            var Q15;
            Q15=makeQuery(id+"F1.opExtrude","SWEPT_BODY",BODY,{"disambiguationData":[OSD([sQuery(id+"F0.wireOp",EDGE,"E121")])]});
            var Q16;
            Q16=makeQuery(id+"F1.opExtrude","SWEPT_BODY",BODY,{"disambiguationData":[OSD([sQuery(id+"F0.wireOp",EDGE,"E123")])]});
            var Q17;
            Q17=makeQuery(id+"F1.opExtrude","SWEPT_BODY",BODY,{"disambiguationData":[OSD([sQuery(id+"F0.wireOp",EDGE,"E124")])]});
            var Q18;
            Q18=makeQuery(id+"F1.opExtrude","SWEPT_BODY",BODY,{"disambiguationData":[OSD([sQuery(id+"F0.wireOp",EDGE,"E125")])]});
            var Q19;
            Q19=makeQuery(id+"F1.opExtrude","SWEPT_BODY",BODY,{"disambiguationData":[OSD([sQuery(id+"F0.wireOp",EDGE,"E126")])]});
            var Q20;
            Q20=makeQuery(id+"F1.opExtrude","SWEPT_BODY",BODY,{"disambiguationData":[OSD([sQuery(id+"F0.wireOp",EDGE,"E127")])]});
            var Q21;
            Q21=makeQuery(id+"F1.opExtrude","SWEPT_BODY",BODY,{"disambiguationData":[OSD([sQuery(id+"F0.wireOp",EDGE,"E128")])]});
            var Q22;
            Q22=makeQuery(id+"F1.opExtrude","SWEPT_BODY",BODY,{"disambiguationData":[OSD([sQuery(id+"F0.wireOp",EDGE,"E129")])]});
            var Q23;
            Q23=makeQuery(id+"F1.opExtrude","SWEPT_BODY",BODY,{"disambiguationData":[OSD([sQuery(id+"F0.wireOp",EDGE,"E130")])]});
            var Q24;
            Q24=makeQuery(id+"F1.opExtrude","SWEPT_BODY",BODY,{"disambiguationData":[OSD([sQuery(id+"F0.wireOp",EDGE,"E131")])]});
            var Q25;
            Q25=makeQuery(id+"F1.opExtrude","SWEPT_BODY",BODY,{"disambiguationData":[OSD([sQuery(id+"F0.wireOp",EDGE,"E132")])]});
            var Q26;
            Q26=makeQuery(id+"F1.opExtrude","SWEPT_BODY",BODY,{"disambiguationData":[OSD([sQuery(id+"F0.wireOp",EDGE,"E133")])]});
            var Q27;
            Q27=makeQuery(id+"F1.opExtrude","SWEPT_BODY",BODY,{"disambiguationData":[OSD([sQuery(id+"F0.wireOp",EDGE,"E134")])]});
            var Q28;
            Q28=makeQuery(id+"F1.opExtrude","SWEPT_BODY",BODY,{"disambiguationData":[OSD([sQuery(id+"F0.wireOp",EDGE,"E135")])]});
            var Q29;
            Q29=makeQuery(id+"F1.opExtrude","SWEPT_BODY",BODY,{"disambiguationData":[OSD([sQuery(id+"F0.wireOp",EDGE,"E136")])]});
            var Q30;
            Q30=makeQuery(id+"F1.opExtrude","SWEPT_BODY",BODY,{"disambiguationData":[OSD([sQuery(id+"F0.wireOp",EDGE,"E137")])]});
            var Q31;
            Q31=makeQuery(id+"F1.opExtrude","SWEPT_BODY",BODY,{"disambiguationData":[OSD([sQuery(id+"F0.wireOp",EDGE,"E138")])]});
            var Q32;
            Q32=makeQuery(id+"F1.opExtrude","SWEPT_BODY",BODY,{"disambiguationData":[OSD([sQuery(id+"F0.wireOp",EDGE,"E139")])]});
            var Q33;
            Q33=makeQuery(id+"F1.opExtrude","SWEPT_BODY",BODY,{"disambiguationData":[OSD([sQuery(id+"F0.wireOp",EDGE,"E140")])]});
            var Q34;
            Q34=makeQuery(id+"F1.opExtrude","SWEPT_BODY",BODY,{"disambiguationData":[OSD([sQuery(id+"F0.wireOp",EDGE,"E141")])]});
            var Q35;
            Q35=makeQuery(id+"F1.opExtrude","SWEPT_BODY",BODY,{"disambiguationData":[OSD([sQuery(id+"F0.wireOp",EDGE,"E142")])]});
            var Q36;
            Q36=makeQuery(id+"F1.opExtrude","SWEPT_BODY",BODY,{"disambiguationData":[OSD([sQuery(id+"F0.wireOp",EDGE,"E143")])]});
            var Q37;
            Q37=makeQuery(id+"F1.opExtrude","SWEPT_BODY",BODY,{"disambiguationData":[OSD([sQuery(id+"F0.wireOp",EDGE,"E144")])]});
            var Q38;
            Q38=makeQuery(id+"F1.opExtrude","SWEPT_BODY",BODY,{"disambiguationData":[OSD([sQuery(id+"F0.wireOp",EDGE,"E145")])]});
            var Q39;
            Q39=makeQuery(id+"F1.opExtrude","SWEPT_BODY",BODY,{"disambiguationData":[OSD([sQuery(id+"F0.wireOp",EDGE,"E146")])]});
            var Q40;
            Q40=makeQuery(id+"F1.opExtrude","SWEPT_BODY",BODY,{"disambiguationData":[OSD([sQuery(id+"F0.wireOp",EDGE,"E147")])]});
            var Q41;
            Q41=makeQuery(id+"F1.opExtrude","SWEPT_BODY",BODY,{"disambiguationData":[OSD([sQuery(id+"F0.wireOp",EDGE,"E149")])]});
            var Q42;
            Q42=makeQuery(id+"F1.opExtrude","SWEPT_BODY",BODY,{"disambiguationData":[OSD([sQuery(id+"F0.wireOp",EDGE,"E150")])]});
            var Q43;
            Q43=makeQuery(id+"F1.opExtrude","SWEPT_BODY",BODY,{"disambiguationData":[OSD([sQuery(id+"F0.wireOp",EDGE,"E151")])]});
            var Q44;
            Q44=makeQuery(id+"F1.opExtrude","SWEPT_BODY",BODY,{"disambiguationData":[OSD([sQuery(id+"F0.wireOp",EDGE,"E152")])]});
            var Q45;
            Q45=makeQuery(id+"F1.opExtrude","SWEPT_BODY",BODY,{"disambiguationData":[OSD([sQuery(id+"F0.wireOp",EDGE,"E153")])]});
            var Q46;
            Q46=makeQuery(id+"F1.opExtrude","SWEPT_BODY",BODY,{"disambiguationData":[OSD([sQuery(id+"F0.wireOp",EDGE,"E154")])]});
            var Q47;
            Q47=makeQuery(id+"F1.opExtrude","SWEPT_BODY",BODY,{"disambiguationData":[OSD([sQuery(id+"F0.wireOp",EDGE,"E155")])]});
            var Q48;
            Q48=makeQuery(id+"F1.opExtrude","SWEPT_BODY",BODY,{"disambiguationData":[OSD([sQuery(id+"F0.wireOp",EDGE,"E156")])]});
            var Q49;
            Q49=makeQuery(id+"F1.opExtrude","SWEPT_BODY",BODY,{"disambiguationData":[OSD([sQuery(id+"F0.wireOp",EDGE,"E157")])]});
            var Q50;
            Q50=makeQuery(id+"F1.opExtrude","SWEPT_BODY",BODY,{"disambiguationData":[OSD([sQuery(id+"F0.wireOp",EDGE,"E158")])]});
            var Q51;
            Q51=makeQuery(id+"F1.opExtrude","SWEPT_BODY",BODY,{"disambiguationData":[OSD([sQuery(id+"F0.wireOp",EDGE,"E159")])]});
            var Q52;
            Q52=makeQuery(id+"F1.opExtrude","SWEPT_BODY",BODY,{"disambiguationData":[OSD([sQuery(id+"F0.wireOp",EDGE,"E160")])]});
            var Q53;
            Q53=makeQuery(id+"F1.opExtrude","SWEPT_BODY",BODY,{"disambiguationData":[OSD([sQuery(id+"F0.wireOp",EDGE,"E161")])]});
            var Q54;
            Q54=makeQuery(id+"F1.opExtrude","SWEPT_BODY",BODY,{"disambiguationData":[OSD([sQuery(id+"F0.wireOp",EDGE,"E162")])]});
            var Q55;
            Q55=makeQuery(id+"F1.opExtrude","SWEPT_BODY",BODY,{"disambiguationData":[OSD([sQuery(id+"F0.wireOp",EDGE,"E163")])]});
            var Q56;
            Q56=makeQuery(id+"F1.opExtrude","SWEPT_BODY",BODY,{"disambiguationData":[OSD([sQuery(id+"F0.wireOp",EDGE,"E164")])]});
            var Q57;
            Q57=makeQuery(id+"F1.opExtrude","SWEPT_BODY",BODY,{"disambiguationData":[OSD([sQuery(id+"F0.wireOp",EDGE,"E165")])]});
            var Q58;
            Q58=sQuery(id+"F0.wireOp",VERTEX,"E109.center");
            transform(context, id + "F5", {"entities" : qUnion([Q0, Q1, Q2, Q3, Q4, Q5, Q6, Q7, Q8, Q9, Q10, Q11, Q12, Q13, Q14, Q15, Q16, Q17, Q18, Q19, Q20, Q21, Q22, Q23, Q24, Q25, Q26, Q27, Q28, Q29, Q30, Q31, Q32, Q33, Q34, Q35, Q36, Q37, Q38, Q39, Q40, Q41, Q42, Q43, Q44, Q45, Q46, Q47, Q48, Q49, Q50, Q51, Q52, Q53, Q54, Q55, Q56, Q57]), "transformType" : TransformType.SCALE_UNIFORMLY, "scale" : 1.15, "scalePoint" : qUnion([Q58]), "makeCopy" : false});
        }
        {
            var Q0;
            Q0=qCreatedBy(makeId("Front.planeOp"),FACE);
            var sketch = newSketch(context, id + "F6", { "sketchPlane" : qUnion([Q0])});
            skLineSegment(sketch, "E166.bottom", {"start": v(-74.69, 97.47) * mm, "end": v(76.7, 97.47) * mm});
            skLineSegment(sketch, "E166.top", {"start": v(-74.69, 72.07) * mm, "end": v(76.7, 72.07) * mm});
            skLineSegment(sketch, "E166.left", {"start": v(-74.69, 97.47) * mm, "end": v(-74.69, 72.07) * mm});
            skLineSegment(sketch, "E166.right", {"start": v(76.7, 97.47) * mm, "end": v(76.7, 72.07) * mm});
            skSolve(sketch);
        }
        {
            var Q0;
            Q0=makeQuery(id+"F6.imprint","IMPRINT",FACE,{"disambiguationData":[TD([[makeQuery(id+"F6.imprint","IMPRINT",EDGE,{"derivedFrom":sQuery(id+"F6.wireOp",EDGE,"E166.bottom")}),-1.0]])]});
            extrude(context, id + "F7", {"entities" : qUnion([Q0]), "oppositeDirection" : true, "depth" : 1.27 * mm});
        }
    });
